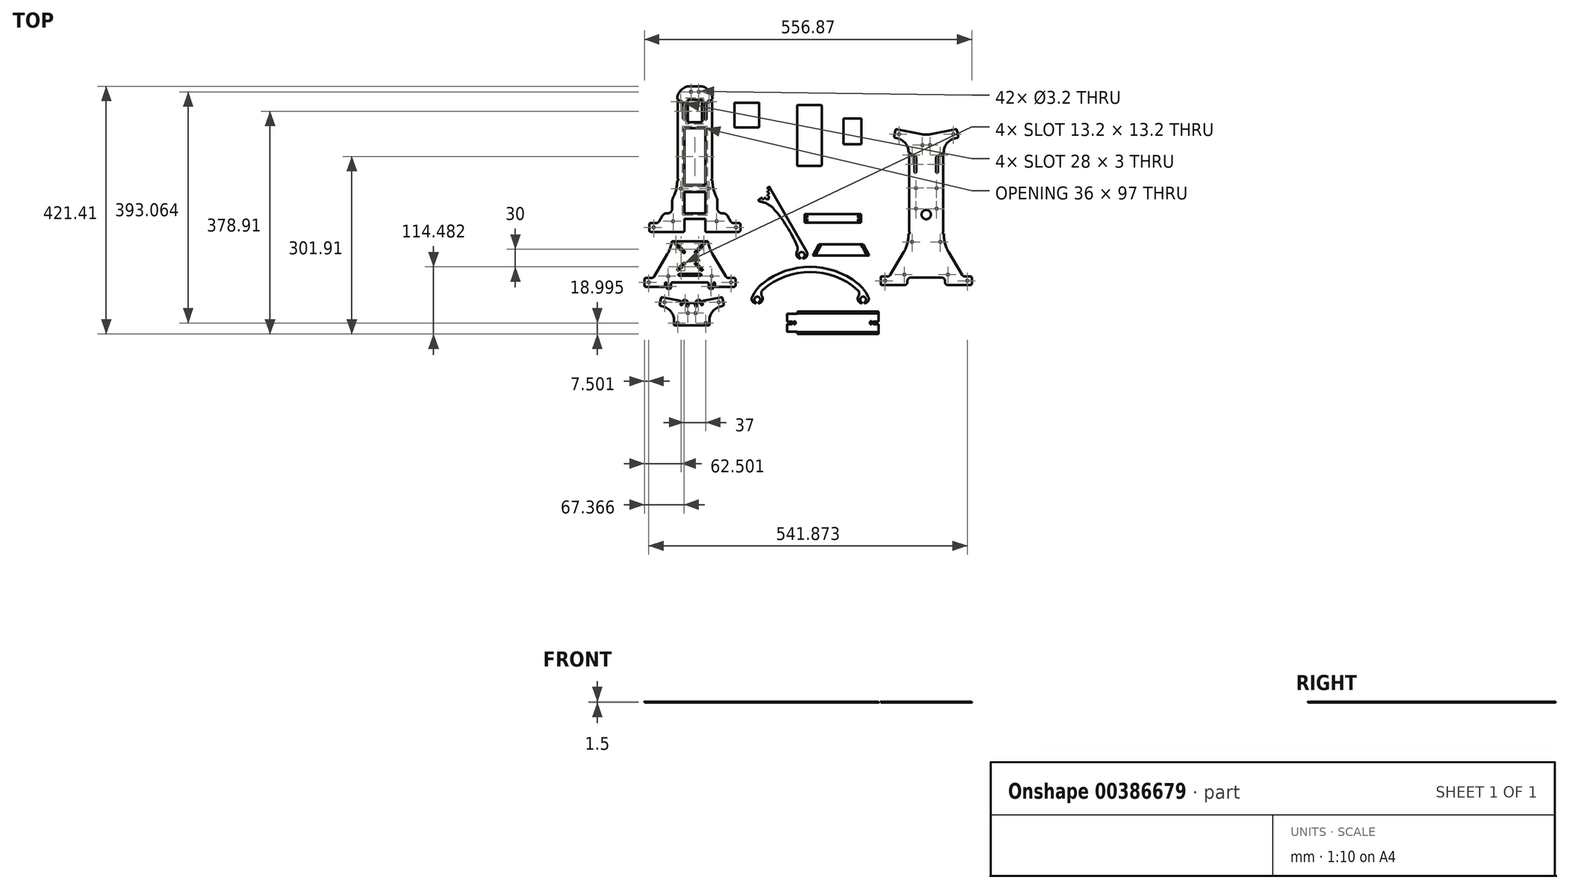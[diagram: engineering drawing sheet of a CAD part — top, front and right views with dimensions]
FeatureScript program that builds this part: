
annotation { "Feature Type Name" : "Feature", "Feature Type Description" : "" }
export const myFeature = defineFeature(function(context is Context, id is Id, definition is map)
    precondition{}
    {
        {
            var Q0;
            Q0=qCreatedBy(makeId("Top.planeOp"),FACE);
            var sketch = newSketch(context, id + "F0", { "sketchPlane" : qUnion([Q0])});
            skCircle(sketch, "E0", {"center": v(204.33, 96.17) * mm, "radius": 1.6 * mm});
            skCircle(sketch, "E1", {"center": v(204.33, 61.17) * mm, "radius": 1.6 * mm});
            skCircle(sketch, "E2", {"center": v(162.83, 152.67) * mm, "radius": 1.6 * mm});
            skCircle(sketch, "E3", {"center": v(162.83, 4.67) * mm, "radius": 1.6 * mm});
            skCircle(sketch, "E4", {"center": v(186.83, 51.17) * mm, "radius": 8 * mm});
            skCircle(sketch, "E5", {"center": v(180.33, 169.32) * mm, "radius": 1.6 * mm});
            skCircle(sketch, "E6", {"center": v(193.33, 169.32) * mm, "radius": 1.6 * mm});
            skCircle(sketch, "E7", {"center": v(223.83, -50.83) * mm, "radius": 1.6 * mm});
            skCircle(sketch, "E8", {"center": v(233, 187.9) * mm, "radius": 1.6 * mm});
            skCircle(sketch, "E9", {"center": v(140.66, 187.9) * mm, "radius": 1.6 * mm});
            skLineSegment(sketch, "E10", {"start": v(154.83, -63.83) * mm, "end": v(154.83, -63.83) * mm});
            skArc(sketch, "E11", {"start": v(149.83, -68.83) * mm, "mid": v(153.37, -67.36) * mm, "end": v(154.83, -63.83) * mm});
            skLineSegment(sketch, "E12", {"start": v(111.83, -68.83) * mm, "end": v(149.83, -68.83) * mm});
            skArc(sketch, "E13", {"start": v(109.33, -66.33) * mm, "mid": v(110.07, -68.1) * mm, "end": v(111.83, -68.83) * mm});
            skLineSegment(sketch, "E14", {"start": v(109.33, -56.33) * mm, "end": v(109.33, -66.33) * mm});
            skArc(sketch, "E15", {"start": v(111.83, -53.83) * mm, "mid": v(110.07, -54.56) * mm, "end": v(109.33, -56.33) * mm});
            skLineSegment(sketch, "E16", {"start": v(121.48, -53.83) * mm, "end": v(111.83, -53.83) * mm});
            skArc(sketch, "E17", {"start": v(121.48, -53.83) * mm, "mid": v(123.96, -53.17) * mm, "end": v(125.78, -51.37) * mm});
            skLineSegment(sketch, "E18", {"start": v(148.49, -12.95) * mm, "end": v(125.78, -51.37) * mm});
            skArc(sketch, "E19", {"start": v(148.49, -12.95) * mm, "mid": v(154.7, 1.76) * mm, "end": v(156.83, 17.58) * mm});
            skLineSegment(sketch, "E20", {"start": v(156.83, 18.67) * mm, "end": v(156.83, 17.58) * mm});
            skLineSegment(sketch, "E21", {"start": v(157.88, 18.67) * mm, "end": v(156.83, 18.67) * mm});
            skArc(sketch, "E22", {"start": v(157.88, 18.67) * mm, "mid": v(158.63, 18.98) * mm, "end": v(158.93, 19.72) * mm});
            skLineSegment(sketch, "E23", {"start": v(158.93, 19.82) * mm, "end": v(158.93, 19.72) * mm});
            skArc(sketch, "E24", {"start": v(158.93, 19.82) * mm, "mid": v(158.63, 20.57) * mm, "end": v(157.88, 20.87) * mm});
            skLineSegment(sketch, "E25", {"start": v(157.83, 20.87) * mm, "end": v(157.88, 20.87) * mm});
            skLineSegment(sketch, "E26", {"start": v(157.83, 154.47) * mm, "end": v(157.83, 20.87) * mm});
            skLineSegment(sketch, "E27", {"start": v(157.88, 154.47) * mm, "end": v(157.83, 154.47) * mm});
            skArc(sketch, "E28", {"start": v(157.88, 154.47) * mm, "mid": v(158.63, 154.78) * mm, "end": v(158.93, 155.52) * mm});
            skLineSegment(sketch, "E29", {"start": v(158.93, 155.62) * mm, "end": v(158.93, 155.52) * mm});
            skArc(sketch, "E30", {"start": v(158.93, 155.62) * mm, "mid": v(158.63, 156.37) * mm, "end": v(157.88, 156.67) * mm});
            skLineSegment(sketch, "E31", {"start": v(156.83, 156.67) * mm, "end": v(157.88, 156.67) * mm});
            skLineSegment(sketch, "E32", {"start": v(156.83, 157.35) * mm, "end": v(156.83, 156.67) * mm});
            skArc(sketch, "E33", {"start": v(156.83, 157.35) * mm, "mid": v(151.4, 172.57) * mm, "end": v(137.54, 180.88) * mm});
            skLineSegment(sketch, "E34", {"start": v(134.28, 181.54) * mm, "end": v(137.54, 180.88) * mm});
            skArc(sketch, "E35", {"start": v(132.32, 184.48) * mm, "mid": v(132.7, 182.6) * mm, "end": v(134.28, 181.54) * mm});
            skLineSegment(sketch, "E36", {"start": v(134.28, 194.28) * mm, "end": v(132.32, 184.48) * mm});
            skArc(sketch, "E37", {"start": v(137.23, 196.24) * mm, "mid": v(135.35, 195.87) * mm, "end": v(134.28, 194.28) * mm});
            skLineSegment(sketch, "E38", {"start": v(178.99, 187.9) * mm, "end": v(137.23, 196.24) * mm});
            skArc(sketch, "E39", {"start": v(178.99, 187.9) * mm, "mid": v(186.83, 187.12) * mm, "end": v(194.68, 187.9) * mm});
            skLineSegment(sketch, "E40", {"start": v(236.44, 196.24) * mm, "end": v(194.68, 187.9) * mm});
            skArc(sketch, "E41", {"start": v(239.38, 194.28) * mm, "mid": v(238.32, 195.87) * mm, "end": v(236.44, 196.24) * mm});
            skLineSegment(sketch, "E42", {"start": v(241.34, 184.48) * mm, "end": v(239.38, 194.28) * mm});
            skArc(sketch, "E43", {"start": v(239.38, 181.54) * mm, "mid": v(240.97, 182.6) * mm, "end": v(241.34, 184.48) * mm});
            skLineSegment(sketch, "E44", {"start": v(236.13, 180.88) * mm, "end": v(239.38, 181.54) * mm});
            skArc(sketch, "E45", {"start": v(236.13, 180.88) * mm, "mid": v(222.27, 172.57) * mm, "end": v(216.83, 157.35) * mm});
            skLineSegment(sketch, "E46", {"start": v(216.83, 156.67) * mm, "end": v(216.83, 157.35) * mm});
            skLineSegment(sketch, "E47", {"start": v(215.78, 156.67) * mm, "end": v(216.83, 156.67) * mm});
            skArc(sketch, "E48", {"start": v(215.78, 156.67) * mm, "mid": v(215.04, 156.37) * mm, "end": v(214.73, 155.62) * mm});
            skLineSegment(sketch, "E49", {"start": v(214.73, 155.52) * mm, "end": v(214.73, 155.62) * mm});
            skArc(sketch, "E50", {"start": v(214.73, 155.52) * mm, "mid": v(215.04, 154.78) * mm, "end": v(215.78, 154.47) * mm});
            skLineSegment(sketch, "E51", {"start": v(215.83, 154.47) * mm, "end": v(215.78, 154.47) * mm});
            skLineSegment(sketch, "E52", {"start": v(215.83, 20.87) * mm, "end": v(215.83, 154.47) * mm});
            skLineSegment(sketch, "E53", {"start": v(215.78, 20.87) * mm, "end": v(215.83, 20.87) * mm});
            skArc(sketch, "E54", {"start": v(215.78, 20.87) * mm, "mid": v(215.04, 20.57) * mm, "end": v(214.73, 19.82) * mm});
            skLineSegment(sketch, "E55", {"start": v(214.73, 19.72) * mm, "end": v(214.73, 19.82) * mm});
            skArc(sketch, "E56", {"start": v(214.73, 19.72) * mm, "mid": v(215.04, 18.98) * mm, "end": v(215.78, 18.67) * mm});
            skLineSegment(sketch, "E57", {"start": v(216.83, 18.67) * mm, "end": v(215.78, 18.67) * mm});
            skLineSegment(sketch, "E58", {"start": v(216.83, 17.58) * mm, "end": v(216.83, 18.67) * mm});
            skArc(sketch, "E59", {"start": v(216.83, 17.58) * mm, "mid": v(218.96, 1.76) * mm, "end": v(225.18, -12.95) * mm});
            skLineSegment(sketch, "E60", {"start": v(247.88, -51.37) * mm, "end": v(225.18, -12.95) * mm});
            skArc(sketch, "E61", {"start": v(247.88, -51.37) * mm, "mid": v(249.7, -53.17) * mm, "end": v(252.19, -53.83) * mm});
            skLineSegment(sketch, "E62", {"start": v(261.83, -53.83) * mm, "end": v(252.19, -53.83) * mm});
            skArc(sketch, "E63", {"start": v(264.33, -56.33) * mm, "mid": v(263.6, -54.56) * mm, "end": v(261.83, -53.83) * mm});
            skLineSegment(sketch, "E64", {"start": v(264.33, -66.33) * mm, "end": v(264.33, -56.33) * mm});
            skArc(sketch, "E65", {"start": v(261.83, -68.83) * mm, "mid": v(263.6, -68.1) * mm, "end": v(264.33, -66.33) * mm});
            skLineSegment(sketch, "E66", {"start": v(223.83, -68.83) * mm, "end": v(261.83, -68.83) * mm});
            skArc(sketch, "E67", {"start": v(218.83, -63.83) * mm, "mid": v(220.3, -67.36) * mm, "end": v(223.83, -68.83) * mm});
            skCircle(sketch, "E68", {"center": v(116.83, -61.33) * mm, "radius": 1.6 * mm});
            skCircle(sketch, "E69", {"center": v(256.83, -61.33) * mm, "radius": 1.6 * mm});
            skCircle(sketch, "E70", {"center": v(149.83, -50.83) * mm, "radius": 1.6 * mm});
            skLineSegment(sketch, "E71", {"start": v(203.83, 148.67) * mm, "end": v(203.83, 123.67) * mm});
            skArc(sketch, "E72", {"start": v(203.83, 123.67) * mm, "mid": v(205.33, 122.17) * mm, "end": v(206.83, 123.67) * mm});
            skLineSegment(sketch, "E73", {"start": v(206.83, 123.67) * mm, "end": v(206.83, 148.67) * mm});
            skArc(sketch, "E74", {"start": v(206.83, 148.67) * mm, "mid": v(205.33, 150.17) * mm, "end": v(203.83, 148.67) * mm});
            skLineSegment(sketch, "E75", {"start": v(169.83, 123.67) * mm, "end": v(169.83, 148.67) * mm});
            skArc(sketch, "E76", {"start": v(169.83, 148.67) * mm, "mid": v(168.33, 150.17) * mm, "end": v(166.83, 148.67) * mm});
            skLineSegment(sketch, "E77", {"start": v(166.83, 148.67) * mm, "end": v(166.83, 123.67) * mm});
            skArc(sketch, "E78", {"start": v(166.83, 123.67) * mm, "mid": v(168.33, 122.17) * mm, "end": v(169.83, 123.67) * mm});
            skCircle(sketch, "E79", {"center": v(210.83, 4.67) * mm, "radius": 1.6 * mm});
            skCircle(sketch, "E80", {"center": v(210.83, 152.67) * mm, "radius": 1.6 * mm});
            skCircle(sketch, "E81", {"center": v(169.33, 61.17) * mm, "radius": 1.6 * mm});
            skCircle(sketch, "E82", {"center": v(169.33, 96.17) * mm, "radius": 1.6 * mm});
            skArc(sketch, "E83", {"start": v(-8.67, 134.54) * mm, "mid": v(-8.32, 133.7) * mm, "end": v(-7.47, 133.34) * mm});
            skLineSegment(sketch, "E84", {"start": v(14.13, 133.34) * mm, "end": v(-7.47, 133.34) * mm});
            skLineSegment(sketch, "E85", {"start": v(-7.47, 133.34) * mm, "end": v(14.13, 133.34) * mm});
            skArc(sketch, "E86", {"start": v(14.13, 133.34) * mm, "mid": v(14.97, 133.7) * mm, "end": v(15.33, 134.54) * mm});
            skLineSegment(sketch, "E87", {"start": v(15.33, 170.14) * mm, "end": v(15.33, 134.54) * mm});
            skLineSegment(sketch, "E88", {"start": v(15.33, 134.54) * mm, "end": v(15.33, 170.14) * mm});
            skArc(sketch, "E89", {"start": v(15.33, 170.14) * mm, "mid": v(14.97, 170.99) * mm, "end": v(14.13, 171.34) * mm});
            skLineSegment(sketch, "E90", {"start": v(-7.47, 171.34) * mm, "end": v(14.13, 171.34) * mm});
            skLineSegment(sketch, "E91", {"start": v(14.13, 171.34) * mm, "end": v(-7.47, 171.34) * mm});
            skArc(sketch, "E92", {"start": v(-7.47, 171.34) * mm, "mid": v(-8.32, 170.99) * mm, "end": v(-8.67, 170.14) * mm});
            skLineSegment(sketch, "E93", {"start": v(-8.67, 134.54) * mm, "end": v(-8.67, 170.14) * mm});
            skLineSegment(sketch, "E94", {"start": v(-8.67, 170.14) * mm, "end": v(-8.67, 134.54) * mm});
            skArc(sketch, "E95", {"start": v(-14.67, 27.54) * mm, "mid": v(-14.32, 26.7) * mm, "end": v(-13.47, 26.34) * mm});
            skLineSegment(sketch, "E96", {"start": v(20.13, 26.34) * mm, "end": v(-13.47, 26.34) * mm});
            skLineSegment(sketch, "E97", {"start": v(-13.47, 26.34) * mm, "end": v(20.13, 26.34) * mm});
            skArc(sketch, "E98", {"start": v(20.13, 26.34) * mm, "mid": v(20.97, 26.7) * mm, "end": v(21.33, 27.54) * mm});
            skLineSegment(sketch, "E99", {"start": v(21.33, 122.14) * mm, "end": v(21.33, 27.54) * mm});
            skLineSegment(sketch, "E100", {"start": v(21.33, 27.54) * mm, "end": v(21.33, 122.14) * mm});
            skArc(sketch, "E101", {"start": v(21.33, 122.14) * mm, "mid": v(20.97, 122.99) * mm, "end": v(20.13, 123.34) * mm});
            skLineSegment(sketch, "E102", {"start": v(-13.47, 123.34) * mm, "end": v(20.13, 123.34) * mm});
            skLineSegment(sketch, "E103", {"start": v(20.13, 123.34) * mm, "end": v(-13.47, 123.34) * mm});
            skArc(sketch, "E104", {"start": v(-13.47, 123.34) * mm, "mid": v(-14.32, 122.99) * mm, "end": v(-14.67, 122.14) * mm});
            skLineSegment(sketch, "E105", {"start": v(-14.67, 27.54) * mm, "end": v(-14.67, 122.14) * mm});
            skLineSegment(sketch, "E106", {"start": v(-14.67, 122.14) * mm, "end": v(-14.67, 27.54) * mm});
            skArc(sketch, "E107", {"start": v(-14.67, -20.46) * mm, "mid": v(-14.32, -21.3) * mm, "end": v(-13.47, -21.66) * mm});
            skLineSegment(sketch, "E108", {"start": v(20.13, -21.66) * mm, "end": v(-13.47, -21.66) * mm});
            skLineSegment(sketch, "E109", {"start": v(-13.47, -21.66) * mm, "end": v(20.13, -21.66) * mm});
            skArc(sketch, "E110", {"start": v(20.13, -21.66) * mm, "mid": v(20.97, -21.3) * mm, "end": v(21.33, -20.46) * mm});
            skLineSegment(sketch, "E111", {"start": v(21.33, 13.14) * mm, "end": v(21.33, -20.46) * mm});
            skLineSegment(sketch, "E112", {"start": v(21.33, -20.46) * mm, "end": v(21.33, 13.14) * mm});
            skArc(sketch, "E113", {"start": v(21.33, 13.14) * mm, "mid": v(20.97, 13.99) * mm, "end": v(20.13, 14.34) * mm});
            skLineSegment(sketch, "E114", {"start": v(-13.47, 14.34) * mm, "end": v(20.13, 14.34) * mm});
            skLineSegment(sketch, "E115", {"start": v(20.13, 14.34) * mm, "end": v(-13.47, 14.34) * mm});
            skArc(sketch, "E116", {"start": v(-13.47, 14.34) * mm, "mid": v(-14.32, 13.99) * mm, "end": v(-14.67, 13.14) * mm});
            skLineSegment(sketch, "E117", {"start": v(-14.67, -20.46) * mm, "end": v(-14.67, 13.14) * mm});
            skLineSegment(sketch, "E118", {"start": v(-14.67, 13.14) * mm, "end": v(-14.67, -20.46) * mm});
            skCircle(sketch, "E119", {"center": v(-20.67, 168.34) * mm, "radius": 1.6 * mm});
            skCircle(sketch, "E120", {"center": v(-20.67, 20.34) * mm, "radius": 1.6 * mm});
            skLineSegment(sketch, "E121", {"start": v(-13.67, 139.34) * mm, "end": v(-13.67, 164.34) * mm});
            skArc(sketch, "E122", {"start": v(-13.67, 164.34) * mm, "mid": v(-15.17, 165.84) * mm, "end": v(-16.67, 164.34) * mm});
            skLineSegment(sketch, "E123", {"start": v(-16.67, 164.34) * mm, "end": v(-16.67, 139.34) * mm});
            skArc(sketch, "E124", {"start": v(-16.67, 139.34) * mm, "mid": v(-15.17, 137.84) * mm, "end": v(-13.67, 139.34) * mm});
            skLineSegment(sketch, "E125", {"start": v(20.33, 164.34) * mm, "end": v(20.33, 139.34) * mm});
            skArc(sketch, "E126", {"start": v(20.33, 139.34) * mm, "mid": v(21.83, 137.84) * mm, "end": v(23.33, 139.34) * mm});
            skLineSegment(sketch, "E127", {"start": v(23.33, 139.34) * mm, "end": v(23.33, 164.34) * mm});
            skArc(sketch, "E128", {"start": v(23.33, 164.34) * mm, "mid": v(21.83, 165.84) * mm, "end": v(20.33, 164.34) * mm});
            skCircle(sketch, "E129", {"center": v(-33.67, -35.16) * mm, "radius": 1.6 * mm});
            skCircle(sketch, "E130", {"center": v(73.33, -45.66) * mm, "radius": 1.6 * mm});
            skLineSegment(sketch, "E131", {"start": v(11.33, 194.34) * mm, "end": v(-4.67, 194.34) * mm});
            skLineSegment(sketch, "E132", {"start": v(-26.67, 172.34) * mm, "end": v(-25.62, 172.34) * mm});
            skArc(sketch, "E133", {"start": v(-4.67, 194.34) * mm, "mid": v(-20.23, 187.9) * mm, "end": v(-26.67, 172.34) * mm});
            skLineSegment(sketch, "E134", {"start": v(-24.57, 171.3) * mm, "end": v(-24.57, 171.2) * mm});
            skArc(sketch, "E135", {"start": v(-24.57, 171.3) * mm, "mid": v(-24.88, 172.03) * mm, "end": v(-25.62, 172.34) * mm});
            skLineSegment(sketch, "E136", {"start": v(-25.62, 170.14) * mm, "end": v(-25.67, 170.14) * mm});
            skArc(sketch, "E137", {"start": v(-25.62, 170.14) * mm, "mid": v(-24.88, 170.45) * mm, "end": v(-24.57, 171.2) * mm});
            skLineSegment(sketch, "E138", {"start": v(-25.67, 170.14) * mm, "end": v(-25.67, 36.54) * mm});
            skLineSegment(sketch, "E139", {"start": v(-25.67, 36.54) * mm, "end": v(-25.62, 36.54) * mm});
            skLineSegment(sketch, "E140", {"start": v(-24.57, 35.5) * mm, "end": v(-24.57, 35.4) * mm});
            skArc(sketch, "E141", {"start": v(-24.57, 35.5) * mm, "mid": v(-24.88, 36.23) * mm, "end": v(-25.62, 36.54) * mm});
            skLineSegment(sketch, "E142", {"start": v(-25.62, 34.34) * mm, "end": v(-26.67, 34.34) * mm});
            skArc(sketch, "E143", {"start": v(-25.62, 34.34) * mm, "mid": v(-24.88, 34.65) * mm, "end": v(-24.57, 35.4) * mm});
            skLineSegment(sketch, "E144", {"start": v(-26.67, 34.34) * mm, "end": v(-26.67, 33.24) * mm});
            skArc(sketch, "E145", {"start": v(-34.04, 4.44) * mm, "mid": v(-28.54, 18.38) * mm, "end": v(-26.67, 33.24) * mm});
            skLineSegment(sketch, "E146", {"start": v(-35.02, 0.6) * mm, "end": v(-35.02, -13.66) * mm});
            skArc(sketch, "E147", {"start": v(-34.04, 4.44) * mm, "mid": v(-34.77, 2.59) * mm, "end": v(-35.02, 0.6) * mm});
            skLineSegment(sketch, "E148", {"start": v(-43.02, -21.66) * mm, "end": v(-44.86, -21.66) * mm});
            skArc(sketch, "E149", {"start": v(-43.02, -21.66) * mm, "mid": v(-37.36, -19.32) * mm, "end": v(-35.02, -13.66) * mm});
            skLineSegment(sketch, "E150", {"start": v(-51.75, -25.59) * mm, "end": v(-57.72, -35.7) * mm});
            skArc(sketch, "E151", {"start": v(-44.86, -21.66) * mm, "mid": v(-48.82, -22.71) * mm, "end": v(-51.75, -25.59) * mm});
            skLineSegment(sketch, "E152", {"start": v(-62.03, -38.16) * mm, "end": v(-71.67, -38.16) * mm});
            skArc(sketch, "E153", {"start": v(-62.03, -38.16) * mm, "mid": v(-59.55, -37.5) * mm, "end": v(-57.72, -35.7) * mm});
            skLineSegment(sketch, "E154", {"start": v(-74.17, -40.66) * mm, "end": v(-74.17, -50.66) * mm});
            skArc(sketch, "E155", {"start": v(-71.67, -38.16) * mm, "mid": v(-73.44, -38.9) * mm, "end": v(-74.17, -40.66) * mm});
            skLineSegment(sketch, "E156", {"start": v(-71.67, -53.16) * mm, "end": v(-15.87, -53.16) * mm});
            skArc(sketch, "E157", {"start": v(-74.17, -50.66) * mm, "mid": v(-73.44, -52.43) * mm, "end": v(-71.67, -53.16) * mm});
            skLineSegment(sketch, "E158", {"start": v(-14.67, -51.96) * mm, "end": v(-14.67, -32.36) * mm});
            skArc(sketch, "E159", {"start": v(-15.87, -53.16) * mm, "mid": v(-15.03, -52.8) * mm, "end": v(-14.67, -51.96) * mm});
            skLineSegment(sketch, "E160", {"start": v(-13.47, -31.16) * mm, "end": v(20.13, -31.16) * mm});
            skArc(sketch, "E161", {"start": v(-13.47, -31.16) * mm, "mid": v(-14.32, -31.51) * mm, "end": v(-14.67, -32.36) * mm});
            skLineSegment(sketch, "E162", {"start": v(21.33, -32.36) * mm, "end": v(21.33, -51.96) * mm});
            skArc(sketch, "E163", {"start": v(21.33, -32.36) * mm, "mid": v(20.97, -31.51) * mm, "end": v(20.13, -31.16) * mm});
            skLineSegment(sketch, "E164", {"start": v(22.53, -53.16) * mm, "end": v(78.33, -53.16) * mm});
            skArc(sketch, "E165", {"start": v(21.33, -51.96) * mm, "mid": v(21.68, -52.8) * mm, "end": v(22.53, -53.16) * mm});
            skLineSegment(sketch, "E166", {"start": v(80.83, -50.66) * mm, "end": v(80.83, -40.66) * mm});
            skArc(sketch, "E167", {"start": v(78.33, -53.16) * mm, "mid": v(80.1, -52.43) * mm, "end": v(80.83, -50.66) * mm});
            skLineSegment(sketch, "E168", {"start": v(78.33, -38.16) * mm, "end": v(68.68, -38.16) * mm});
            skArc(sketch, "E169", {"start": v(80.83, -40.66) * mm, "mid": v(80.1, -38.9) * mm, "end": v(78.33, -38.16) * mm});
            skLineSegment(sketch, "E170", {"start": v(64.37, -35.7) * mm, "end": v(58.4, -25.59) * mm});
            skArc(sketch, "E171", {"start": v(64.37, -35.7) * mm, "mid": v(66.2, -37.5) * mm, "end": v(68.68, -38.16) * mm});
            skLineSegment(sketch, "E172", {"start": v(51.51, -21.66) * mm, "end": v(49.67, -21.66) * mm});
            skArc(sketch, "E173", {"start": v(58.4, -25.59) * mm, "mid": v(55.48, -22.71) * mm, "end": v(51.51, -21.66) * mm});
            skLineSegment(sketch, "E174", {"start": v(41.67, -13.66) * mm, "end": v(41.67, 0.6) * mm});
            skArc(sketch, "E175", {"start": v(41.67, -13.66) * mm, "mid": v(44.01, -19.32) * mm, "end": v(49.67, -21.66) * mm});
            skArc(sketch, "E176", {"start": v(41.67, 0.6) * mm, "mid": v(41.42, 2.59) * mm, "end": v(40.69, 4.44) * mm});
            skLineSegment(sketch, "E177", {"start": v(33.33, 33.24) * mm, "end": v(33.33, 34.34) * mm});
            skArc(sketch, "E178", {"start": v(33.33, 33.24) * mm, "mid": v(35.2, 18.38) * mm, "end": v(40.69, 4.44) * mm});
            skLineSegment(sketch, "E179", {"start": v(33.33, 34.34) * mm, "end": v(32.28, 34.34) * mm});
            skLineSegment(sketch, "E180", {"start": v(31.23, 35.4) * mm, "end": v(31.23, 35.5) * mm});
            skArc(sketch, "E181", {"start": v(31.23, 35.4) * mm, "mid": v(31.53, 34.65) * mm, "end": v(32.28, 34.34) * mm});
            skLineSegment(sketch, "E182", {"start": v(32.28, 36.54) * mm, "end": v(32.33, 36.54) * mm});
            skArc(sketch, "E183", {"start": v(32.28, 36.54) * mm, "mid": v(31.53, 36.23) * mm, "end": v(31.23, 35.5) * mm});
            skLineSegment(sketch, "E184", {"start": v(32.33, 36.54) * mm, "end": v(32.33, 170.14) * mm});
            skLineSegment(sketch, "E185", {"start": v(32.33, 170.14) * mm, "end": v(32.28, 170.14) * mm});
            skLineSegment(sketch, "E186", {"start": v(31.23, 171.2) * mm, "end": v(31.23, 171.3) * mm});
            skArc(sketch, "E187", {"start": v(31.23, 171.2) * mm, "mid": v(31.53, 170.45) * mm, "end": v(32.28, 170.14) * mm});
            skLineSegment(sketch, "E188", {"start": v(32.28, 172.34) * mm, "end": v(33.33, 172.34) * mm});
            skArc(sketch, "E189", {"start": v(32.28, 172.34) * mm, "mid": v(31.53, 172.03) * mm, "end": v(31.23, 171.3) * mm});
            skArc(sketch, "E190", {"start": v(33.33, 172.34) * mm, "mid": v(26.88, 187.9) * mm, "end": v(11.33, 194.34) * mm});
            skCircle(sketch, "E191", {"center": v(-66.67, -45.66) * mm, "radius": 1.6 * mm});
            skCircle(sketch, "E192", {"center": v(40.33, -35.16) * mm, "radius": 1.6 * mm});
            skCircle(sketch, "E193", {"center": v(9.83, 184.99) * mm, "radius": 1.6 * mm});
            skCircle(sketch, "E194", {"center": v(-3.17, 184.99) * mm, "radius": 1.6 * mm});
            skCircle(sketch, "E195", {"center": v(27.33, 20.34) * mm, "radius": 1.6 * mm});
            skCircle(sketch, "E196", {"center": v(27.33, 168.34) * mm, "radius": 1.6 * mm});
            skLineSegment(sketch, "E197", {"start": v(-11.67, 131.54) * mm, "end": v(-11.67, 173.14) * mm});
            skLineSegment(sketch, "E198", {"start": v(17.13, 130.34) * mm, "end": v(-10.47, 130.34) * mm});
            skArc(sketch, "E199", {"start": v(-11.67, 131.54) * mm, "mid": v(-11.32, 130.7) * mm, "end": v(-10.47, 130.34) * mm});
            skLineSegment(sketch, "E200", {"start": v(18.33, 173.14) * mm, "end": v(18.33, 131.54) * mm});
            skArc(sketch, "E201", {"start": v(17.13, 130.34) * mm, "mid": v(17.97, 130.7) * mm, "end": v(18.33, 131.54) * mm});
            skLineSegment(sketch, "E202", {"start": v(-10.47, 174.34) * mm, "end": v(17.13, 174.34) * mm});
            skArc(sketch, "E203", {"start": v(18.33, 173.14) * mm, "mid": v(17.97, 173.99) * mm, "end": v(17.13, 174.34) * mm});
            skArc(sketch, "E204", {"start": v(-10.47, 174.34) * mm, "mid": v(-11.32, 173.99) * mm, "end": v(-11.67, 173.14) * mm});
            skLineSegment(sketch, "E205", {"start": v(24.33, 125.14) * mm, "end": v(24.33, 24.54) * mm});
            skArc(sketch, "E206", {"start": v(23.13, 23.34) * mm, "mid": v(23.97, 23.7) * mm, "end": v(24.33, 24.54) * mm});
            skLineSegment(sketch, "E207", {"start": v(-16.47, 126.34) * mm, "end": v(23.13, 126.34) * mm});
            skArc(sketch, "E208", {"start": v(24.33, 125.14) * mm, "mid": v(23.97, 125.99) * mm, "end": v(23.13, 126.34) * mm});
            skLineSegment(sketch, "E209", {"start": v(-17.67, 24.54) * mm, "end": v(-17.67, 125.14) * mm});
            skArc(sketch, "E210", {"start": v(-16.47, 126.34) * mm, "mid": v(-17.32, 125.99) * mm, "end": v(-17.67, 125.14) * mm});
            skLineSegment(sketch, "E211", {"start": v(23.13, 23.34) * mm, "end": v(-16.47, 23.34) * mm});
            skArc(sketch, "E212", {"start": v(-17.67, 24.54) * mm, "mid": v(-17.32, 23.7) * mm, "end": v(-16.47, 23.34) * mm});
            skLineSegment(sketch, "E213", {"start": v(23.13, -24.66) * mm, "end": v(-16.47, -24.66) * mm});
            skLineSegment(sketch, "E214", {"start": v(24.33, 16.14) * mm, "end": v(24.33, -23.46) * mm});
            skArc(sketch, "E215", {"start": v(23.13, -24.66) * mm, "mid": v(23.97, -24.3) * mm, "end": v(24.33, -23.46) * mm});
            skLineSegment(sketch, "E216", {"start": v(-16.47, 17.34) * mm, "end": v(23.13, 17.34) * mm});
            skArc(sketch, "E217", {"start": v(24.33, 16.14) * mm, "mid": v(23.97, 16.99) * mm, "end": v(23.13, 17.34) * mm});
            skLineSegment(sketch, "E218", {"start": v(-17.67, -23.46) * mm, "end": v(-17.67, 16.14) * mm});
            skArc(sketch, "E219", {"start": v(-16.47, 17.34) * mm, "mid": v(-17.32, 16.99) * mm, "end": v(-17.67, 16.14) * mm});
            skArc(sketch, "E220", {"start": v(-17.67, -23.46) * mm, "mid": v(-17.32, -24.3) * mm, "end": v(-16.47, -24.66) * mm});
            skLineSegment(sketch, "E221", {"start": v(-28.63, -131.82) * mm, "end": v(-28.63, -133.82) * mm});
            skLineSegment(sketch, "E222", {"start": v(-25.43, -133.82) * mm, "end": v(-25.43, -131.82) * mm});
            skArc(sketch, "E223", {"start": v(-28.63, -133.82) * mm, "mid": v(-27.03, -135.42) * mm, "end": v(-25.43, -133.82) * mm});
            skLineSegment(sketch, "E224", {"start": v(104.57, -133.82) * mm, "end": v(104.57, -131.82) * mm});
            skArc(sketch, "E225", {"start": v(-25.43, -131.82) * mm, "mid": v(-27.03, -130.22) * mm, "end": v(-28.63, -131.82) * mm});
            skLineSegment(sketch, "E226", {"start": v(101.37, -131.82) * mm, "end": v(101.37, -133.82) * mm});
            skArc(sketch, "E227", {"start": v(104.57, -131.82) * mm, "mid": v(102.97, -130.22) * mm, "end": v(101.37, -131.82) * mm});
            skArc(sketch, "E228", {"start": v(101.37, -133.82) * mm, "mid": v(102.97, -135.42) * mm, "end": v(104.57, -133.82) * mm});
            skLineSegment(sketch, "E229", {"start": v(115.97, -117.07) * mm, "end": v(-22.26, -117.07) * mm});
            skArc(sketch, "E230", {"start": v(-23.23, -117.57) * mm, "mid": v(-22.69, -117.44) * mm, "end": v(-22.26, -117.07) * mm});
            skLineSegment(sketch, "E231", {"start": v(115.97, -129.37) * mm, "end": v(115.97, -117.07) * mm});
            skLineSegment(sketch, "E232", {"start": v(107.97, -130.57) * mm, "end": v(114.77, -130.57) * mm});
            skArc(sketch, "E233", {"start": v(114.77, -130.57) * mm, "mid": v(115.61, -130.22) * mm, "end": v(115.97, -129.37) * mm});
            skLineSegment(sketch, "E234", {"start": v(114.77, -135.07) * mm, "end": v(107.97, -135.07) * mm});
            skArc(sketch, "E235", {"start": v(107.97, -130.57) * mm, "mid": v(105.72, -132.82) * mm, "end": v(107.97, -135.07) * mm});
            skLineSegment(sketch, "E236", {"start": v(115.97, -148.57) * mm, "end": v(115.97, -136.27) * mm});
            skArc(sketch, "E237", {"start": v(115.97, -136.27) * mm, "mid": v(115.61, -135.43) * mm, "end": v(114.77, -135.07) * mm});
            skLineSegment(sketch, "E238", {"start": v(-22.26, -148.57) * mm, "end": v(115.97, -148.57) * mm});
            skLineSegment(sketch, "E239", {"start": v(-38.83, -148.07) * mm, "end": v(-23.23, -148.07) * mm});
            skArc(sketch, "E240", {"start": v(-22.26, -148.57) * mm, "mid": v(-22.69, -148.2) * mm, "end": v(-23.23, -148.07) * mm});
            skLineSegment(sketch, "E241", {"start": v(-40.03, -136.27) * mm, "end": v(-40.03, -146.87) * mm});
            skArc(sketch, "E242", {"start": v(-40.03, -146.87) * mm, "mid": v(-39.68, -147.72) * mm, "end": v(-38.83, -148.07) * mm});
            skLineSegment(sketch, "E243", {"start": v(-32.03, -135.07) * mm, "end": v(-38.83, -135.07) * mm});
            skArc(sketch, "E244", {"start": v(-38.83, -135.07) * mm, "mid": v(-39.68, -135.43) * mm, "end": v(-40.03, -136.27) * mm});
            skLineSegment(sketch, "E245", {"start": v(-38.83, -130.57) * mm, "end": v(-32.03, -130.57) * mm});
            skArc(sketch, "E246", {"start": v(-32.03, -135.07) * mm, "mid": v(-29.78, -132.82) * mm, "end": v(-32.03, -130.57) * mm});
            skLineSegment(sketch, "E247", {"start": v(-40.03, -118.77) * mm, "end": v(-40.03, -129.37) * mm});
            skArc(sketch, "E248", {"start": v(-40.03, -129.37) * mm, "mid": v(-39.68, -130.22) * mm, "end": v(-38.83, -130.57) * mm});
            skLineSegment(sketch, "E249", {"start": v(-23.23, -117.57) * mm, "end": v(-38.83, -117.57) * mm});
            skArc(sketch, "E250", {"start": v(-38.83, -117.57) * mm, "mid": v(-39.68, -117.93) * mm, "end": v(-40.03, -118.77) * mm});
            skLineSegment(sketch, "E251", {"start": v(115.97, -115.57) * mm, "end": v(115.97, -114.77) * mm});
            skLineSegment(sketch, "E252", {"start": v(-22.03, -115.57) * mm, "end": v(115.97, -115.57) * mm});
            skLineSegment(sketch, "E253", {"start": v(-22.03, -114.77) * mm, "end": v(-22.03, -115.57) * mm});
            skLineSegment(sketch, "E254", {"start": v(114.77, -113.57) * mm, "end": v(-20.83, -113.57) * mm});
            skArc(sketch, "E255", {"start": v(-20.83, -113.57) * mm, "mid": v(-21.68, -113.93) * mm, "end": v(-22.03, -114.77) * mm});
            skArc(sketch, "E256", {"start": v(115.97, -114.77) * mm, "mid": v(115.61, -113.93) * mm, "end": v(114.77, -113.57) * mm});
            skLineSegment(sketch, "E257", {"start": v(115.97, -129.37) * mm, "end": v(115.97, -114.77) * mm});
            skLineSegment(sketch, "E258", {"start": v(-22.03, -114.77) * mm, "end": v(-22.03, -116.37) * mm});
            skArc(sketch, "E259", {"start": v(-23.23, -117.57) * mm, "mid": v(-22.39, -117.22) * mm, "end": v(-22.03, -116.37) * mm});
            skLineSegment(sketch, "E260", {"start": v(-22.03, -149.27) * mm, "end": v(-22.03, -150.87) * mm});
            skArc(sketch, "E261", {"start": v(-22.03, -149.27) * mm, "mid": v(-22.39, -148.43) * mm, "end": v(-23.23, -148.07) * mm});
            skLineSegment(sketch, "E262", {"start": v(-20.83, -152.07) * mm, "end": v(114.77, -152.07) * mm});
            skArc(sketch, "E263", {"start": v(-22.03, -150.87) * mm, "mid": v(-21.68, -151.72) * mm, "end": v(-20.83, -152.07) * mm});
            skLineSegment(sketch, "E264", {"start": v(115.97, -150.87) * mm, "end": v(115.97, -136.27) * mm});
            skArc(sketch, "E265", {"start": v(114.77, -152.07) * mm, "mid": v(115.61, -151.72) * mm, "end": v(115.97, -150.87) * mm});
            skLineSegment(sketch, "E266", {"start": v(-22.03, -150.07) * mm, "end": v(-22.03, -150.87) * mm});
            skLineSegment(sketch, "E267", {"start": v(115.97, -150.07) * mm, "end": v(-22.03, -150.07) * mm});
            skLineSegment(sketch, "E268", {"start": v(115.97, -150.87) * mm, "end": v(115.97, -150.07) * mm});
            skLineSegment(sketch, "E269", {"start": v(115.97, -115.57) * mm, "end": v(115.97, -117.07) * mm});
            skLineSegment(sketch, "E270", {"start": v(-22.03, -116.37) * mm, "end": v(-22.03, -115.57) * mm});
            skArc(sketch, "E271", {"start": v(-22.26, -117.07) * mm, "mid": v(-22.1, -116.74) * mm, "end": v(-22.03, -116.37) * mm});
            skArc(sketch, "E272", {"start": v(-22.03, -149.27) * mm, "mid": v(-22.1, -148.9) * mm, "end": v(-22.26, -148.57) * mm});
            skLineSegment(sketch, "E273", {"start": v(-22.03, -150.07) * mm, "end": v(-22.03, -149.27) * mm});
            skLineSegment(sketch, "E274", {"start": v(115.97, -148.57) * mm, "end": v(115.97, -150.07) * mm});
            skCircle(sketch, "E275", {"center": v(-209.04, 1.91) * mm, "radius": 1.6 * mm});
            skLineSegment(sketch, "E276", {"start": v(-167.04, -49.59) * mm, "end": v(-203.04, -49.59) * mm});
            skArc(sketch, "E277", {"start": v(-203.04, -49.59) * mm, "mid": v(-204.64, -51.19) * mm, "end": v(-203.04, -52.79) * mm});
            skLineSegment(sketch, "E278", {"start": v(-203.04, -52.79) * mm, "end": v(-167.04, -52.79) * mm});
            skArc(sketch, "E279", {"start": v(-167.04, -52.79) * mm, "mid": v(-165.44, -51.19) * mm, "end": v(-167.04, -49.59) * mm});
            skLineSegment(sketch, "E280", {"start": v(-196.17, -31.46) * mm, "end": v(-206.17, -41.46) * mm});
            skArc(sketch, "E281", {"start": v(-206.17, -41.46) * mm, "mid": v(-206.17, -43.72) * mm, "end": v(-203.9, -43.72) * mm});
            skLineSegment(sketch, "E282", {"start": v(-203.9, -43.72) * mm, "end": v(-193.9, -33.72) * mm});
            skArc(sketch, "E283", {"start": v(-193.9, -33.72) * mm, "mid": v(-193.9, -31.46) * mm, "end": v(-196.17, -31.46) * mm});
            skCircle(sketch, "E284", {"center": v(-222.04, -53.59) * mm, "radius": 1.6 * mm});
            skCircle(sketch, "E285", {"center": v(-148.04, -53.59) * mm, "radius": 1.6 * mm});
            skCircle(sketch, "E286", {"center": v(-255.04, -64.09) * mm, "radius": 1.6 * mm});
            skCircle(sketch, "E287", {"center": v(-149.04, -71.09) * mm, "radius": 1.6 * mm});
            skLineSegment(sketch, "E288", {"start": v(-154.38, 5.91) * mm, "end": v(-215.7, 5.91) * mm});
            skArc(sketch, "E289", {"start": v(-154.38, 5.91) * mm, "mid": v(-151.58, -5.27) * mm, "end": v(-146.7, -15.7) * mm});
            skLineSegment(sketch, "E290", {"start": v(-124, -54.13) * mm, "end": v(-146.7, -15.7) * mm});
            skArc(sketch, "E291", {"start": v(-124, -54.13) * mm, "mid": v(-122.16, -55.93) * mm, "end": v(-119.69, -56.59) * mm});
            skLineSegment(sketch, "E292", {"start": v(-110.04, -56.59) * mm, "end": v(-119.69, -56.59) * mm});
            skArc(sketch, "E293", {"start": v(-107.54, -59.09) * mm, "mid": v(-108.27, -57.32) * mm, "end": v(-110.04, -56.59) * mm});
            skLineSegment(sketch, "E294", {"start": v(-107.54, -69.09) * mm, "end": v(-107.54, -59.09) * mm});
            skArc(sketch, "E295", {"start": v(-110.04, -71.59) * mm, "mid": v(-108.27, -70.86) * mm, "end": v(-107.54, -69.09) * mm});
            skLineSegment(sketch, "E296", {"start": v(-141.34, -71.59) * mm, "end": v(-110.04, -71.59) * mm});
            skArc(sketch, "E297", {"start": v(-142.54, -70.39) * mm, "mid": v(-142.19, -71.24) * mm, "end": v(-141.34, -71.59) * mm});
            skLineSegment(sketch, "E298", {"start": v(-142.54, -65.54) * mm, "end": v(-142.54, -70.39) * mm});
            skArc(sketch, "E299", {"start": v(-142.54, -65.54) * mm, "mid": v(-142.9, -64.69) * mm, "end": v(-143.74, -64.34) * mm});
            skLineSegment(sketch, "E300", {"start": v(-143.84, -64.34) * mm, "end": v(-143.74, -64.34) * mm});
            skArc(sketch, "E301", {"start": v(-143.84, -64.34) * mm, "mid": v(-144.69, -64.69) * mm, "end": v(-145.04, -65.54) * mm});
            skLineSegment(sketch, "E302", {"start": v(-145.04, -72.59) * mm, "end": v(-145.04, -65.54) * mm});
            skArc(sketch, "E303", {"start": v(-147.54, -75.09) * mm, "mid": v(-145.77, -74.36) * mm, "end": v(-145.04, -72.59) * mm});
            skLineSegment(sketch, "E304", {"start": v(-150.54, -75.09) * mm, "end": v(-147.54, -75.09) * mm});
            skArc(sketch, "E305", {"start": v(-153.04, -72.59) * mm, "mid": v(-152.3, -74.36) * mm, "end": v(-150.54, -75.09) * mm});
            skLineSegment(sketch, "E306", {"start": v(-153.04, -66.59) * mm, "end": v(-153.04, -72.59) * mm});
            skArc(sketch, "E307", {"start": v(-153.04, -66.59) * mm, "mid": v(-153.77, -64.82) * mm, "end": v(-155.54, -64.09) * mm});
            skLineSegment(sketch, "E308", {"start": v(-214.54, -64.09) * mm, "end": v(-155.54, -64.09) * mm});
            skArc(sketch, "E309", {"start": v(-214.54, -64.09) * mm, "mid": v(-216.3, -64.82) * mm, "end": v(-217.04, -66.59) * mm});
            skLineSegment(sketch, "E310", {"start": v(-217.04, -72.59) * mm, "end": v(-217.04, -66.59) * mm});
            skArc(sketch, "E311", {"start": v(-219.54, -75.09) * mm, "mid": v(-217.77, -74.36) * mm, "end": v(-217.04, -72.59) * mm});
            skLineSegment(sketch, "E312", {"start": v(-222.54, -75.09) * mm, "end": v(-219.54, -75.09) * mm});
            skArc(sketch, "E313", {"start": v(-225.04, -72.59) * mm, "mid": v(-224.3, -74.36) * mm, "end": v(-222.54, -75.09) * mm});
            skLineSegment(sketch, "E314", {"start": v(-225.04, -65.54) * mm, "end": v(-225.04, -72.59) * mm});
            skArc(sketch, "E315", {"start": v(-225.04, -65.54) * mm, "mid": v(-225.4, -64.69) * mm, "end": v(-226.24, -64.34) * mm});
            skLineSegment(sketch, "E316", {"start": v(-226.34, -64.34) * mm, "end": v(-226.24, -64.34) * mm});
            skArc(sketch, "E317", {"start": v(-226.34, -64.34) * mm, "mid": v(-227.19, -64.69) * mm, "end": v(-227.54, -65.54) * mm});
            skLineSegment(sketch, "E318", {"start": v(-227.54, -70.39) * mm, "end": v(-227.54, -65.54) * mm});
            skArc(sketch, "E319", {"start": v(-228.74, -71.59) * mm, "mid": v(-227.9, -71.24) * mm, "end": v(-227.54, -70.39) * mm});
            skLineSegment(sketch, "E320", {"start": v(-260.04, -71.59) * mm, "end": v(-228.74, -71.59) * mm});
            skArc(sketch, "E321", {"start": v(-262.54, -69.09) * mm, "mid": v(-261.8, -70.86) * mm, "end": v(-260.04, -71.59) * mm});
            skLineSegment(sketch, "E322", {"start": v(-262.54, -59.09) * mm, "end": v(-262.54, -69.09) * mm});
            skArc(sketch, "E323", {"start": v(-260.04, -56.59) * mm, "mid": v(-261.8, -57.32) * mm, "end": v(-262.54, -59.09) * mm});
            skLineSegment(sketch, "E324", {"start": v(-250.4, -56.59) * mm, "end": v(-260.04, -56.59) * mm});
            skArc(sketch, "E325", {"start": v(-250.4, -56.59) * mm, "mid": v(-247.91, -55.93) * mm, "end": v(-246.09, -54.13) * mm});
            skLineSegment(sketch, "E326", {"start": v(-223.38, -15.7) * mm, "end": v(-246.09, -54.13) * mm});
            skArc(sketch, "E327", {"start": v(-223.38, -15.7) * mm, "mid": v(-218.5, -5.27) * mm, "end": v(-215.7, 5.91) * mm});
            skCircle(sketch, "E328", {"center": v(-221.04, -71.09) * mm, "radius": 1.6 * mm});
            skCircle(sketch, "E329", {"center": v(-115.04, -64.09) * mm, "radius": 1.6 * mm});
            skLineSegment(sketch, "E330", {"start": v(-173.9, -13.72) * mm, "end": v(-163.9, -3.72) * mm});
            skArc(sketch, "E331", {"start": v(-163.9, -3.72) * mm, "mid": v(-163.9, -1.46) * mm, "end": v(-166.17, -1.46) * mm});
            skLineSegment(sketch, "E332", {"start": v(-166.17, -1.46) * mm, "end": v(-176.17, -11.46) * mm});
            skArc(sketch, "E333", {"start": v(-176.17, -11.46) * mm, "mid": v(-176.17, -13.72) * mm, "end": v(-173.9, -13.72) * mm});
            skArc(sketch, "E334", {"start": v(-203.9, -1.46) * mm, "mid": v(-206.17, -1.46) * mm, "end": v(-206.17, -3.72) * mm});
            skLineSegment(sketch, "E335", {"start": v(-206.17, -3.72) * mm, "end": v(-196.17, -13.72) * mm});
            skArc(sketch, "E336", {"start": v(-196.17, -13.72) * mm, "mid": v(-193.9, -13.72) * mm, "end": v(-193.9, -11.46) * mm});
            skLineSegment(sketch, "E337", {"start": v(-193.9, -11.46) * mm, "end": v(-203.9, -1.46) * mm});
            skArc(sketch, "E338", {"start": v(-166.17, -43.72) * mm, "mid": v(-163.9, -43.72) * mm, "end": v(-163.9, -41.46) * mm});
            skLineSegment(sketch, "E339", {"start": v(-163.9, -41.46) * mm, "end": v(-173.9, -31.46) * mm});
            skArc(sketch, "E340", {"start": v(-173.9, -31.46) * mm, "mid": v(-176.17, -31.46) * mm, "end": v(-176.17, -33.72) * mm});
            skLineSegment(sketch, "E341", {"start": v(-176.17, -33.72) * mm, "end": v(-166.17, -43.72) * mm});
            skCircle(sketch, "E342", {"center": v(-161.04, 1.91) * mm, "radius": 1.6 * mm});
            skCircle(sketch, "E343", {"center": v(-178, -133.07) * mm, "radius": 1.6 * mm});
            skCircle(sketch, "E344", {"center": v(-195.5, -116.43) * mm, "radius": 1.6 * mm});
            skCircle(sketch, "E345", {"center": v(-155.83, -97.84) * mm, "radius": 1.6 * mm});
            skCircle(sketch, "E346", {"center": v(-248.18, -97.84) * mm, "radius": 1.6 * mm});
            skLineSegment(sketch, "E347", {"start": v(-232, -129.22) * mm, "end": v(-232, -137.07) * mm});
            skArc(sketch, "E348", {"start": v(-232, -129.22) * mm, "mid": v(-237.68, -113.37) * mm, "end": v(-252.1, -104.7) * mm});
            skLineSegment(sketch, "E349", {"start": v(-254.56, -104.21) * mm, "end": v(-252.1, -104.7) * mm});
            skArc(sketch, "E350", {"start": v(-256.52, -101.27) * mm, "mid": v(-256.15, -103.15) * mm, "end": v(-254.56, -104.21) * mm});
            skLineSegment(sketch, "E351", {"start": v(-254.56, -91.47) * mm, "end": v(-256.52, -101.27) * mm});
            skArc(sketch, "E352", {"start": v(-251.62, -89.5) * mm, "mid": v(-253.5, -89.88) * mm, "end": v(-254.56, -91.47) * mm});
            skLineSegment(sketch, "E353", {"start": v(-221.86, -95.46) * mm, "end": v(-251.62, -89.5) * mm});
            skArc(sketch, "E354", {"start": v(-219.9, -98.4) * mm, "mid": v(-220.27, -96.52) * mm, "end": v(-221.86, -95.46) * mm});
            skLineSegment(sketch, "E355", {"start": v(-220.58, -101.83) * mm, "end": v(-219.9, -98.4) * mm});
            skArc(sketch, "E356", {"start": v(-220.58, -101.83) * mm, "mid": v(-219.7, -103.15) * mm, "end": v(-218.37, -102.27) * mm});
            skLineSegment(sketch, "E357", {"start": v(-217.1, -95.9) * mm, "end": v(-218.37, -102.27) * mm});
            skArc(sketch, "E358", {"start": v(-214.16, -93.94) * mm, "mid": v(-216.03, -94.3) * mm, "end": v(-217.1, -95.9) * mm});
            skLineSegment(sketch, "E359", {"start": v(-211.21, -94.53) * mm, "end": v(-214.16, -93.94) * mm});
            skArc(sketch, "E360", {"start": v(-209.25, -97.47) * mm, "mid": v(-209.62, -95.6) * mm, "end": v(-211.21, -94.53) * mm});
            skLineSegment(sketch, "E361", {"start": v(-210.53, -103.84) * mm, "end": v(-209.25, -97.47) * mm});
            skArc(sketch, "E362", {"start": v(-210.53, -103.84) * mm, "mid": v(-209.45, -105.46) * mm, "end": v(-207.83, -104.38) * mm});
            skLineSegment(sketch, "E363", {"start": v(-207.15, -100.95) * mm, "end": v(-207.83, -104.38) * mm});
            skArc(sketch, "E364", {"start": v(-204.2, -98.99) * mm, "mid": v(-206.08, -99.36) * mm, "end": v(-207.15, -100.95) * mm});
            skLineSegment(sketch, "E365", {"start": v(-202.5, -99.33) * mm, "end": v(-204.2, -98.99) * mm});
            skArc(sketch, "E366", {"start": v(-202.5, -99.33) * mm, "mid": v(-202, -99.38) * mm, "end": v(-201.52, -99.33) * mm});
            skLineSegment(sketch, "E367", {"start": v(-199.81, -98.99) * mm, "end": v(-201.52, -99.33) * mm});
            skArc(sketch, "E368", {"start": v(-196.87, -100.95) * mm, "mid": v(-197.94, -99.36) * mm, "end": v(-199.81, -98.99) * mm});
            skLineSegment(sketch, "E369", {"start": v(-196.18, -104.38) * mm, "end": v(-196.87, -100.95) * mm});
            skArc(sketch, "E370", {"start": v(-196.18, -104.38) * mm, "mid": v(-194.57, -105.46) * mm, "end": v(-193.5, -103.84) * mm});
            skLineSegment(sketch, "E371", {"start": v(-194.77, -97.47) * mm, "end": v(-193.5, -103.84) * mm});
            skArc(sketch, "E372", {"start": v(-192.8, -94.53) * mm, "mid": v(-194.4, -95.6) * mm, "end": v(-194.77, -97.47) * mm});
            skLineSegment(sketch, "E373", {"start": v(-189.86, -93.94) * mm, "end": v(-192.8, -94.53) * mm});
            skArc(sketch, "E374", {"start": v(-186.92, -95.9) * mm, "mid": v(-187.98, -94.3) * mm, "end": v(-189.86, -93.94) * mm});
            skLineSegment(sketch, "E375", {"start": v(-185.64, -102.27) * mm, "end": v(-186.92, -95.9) * mm});
            skArc(sketch, "E376", {"start": v(-185.64, -102.27) * mm, "mid": v(-184.32, -103.15) * mm, "end": v(-183.44, -101.83) * mm});
            skLineSegment(sketch, "E377", {"start": v(-184.12, -98.4) * mm, "end": v(-183.44, -101.83) * mm});
            skArc(sketch, "E378", {"start": v(-182.16, -95.46) * mm, "mid": v(-183.75, -96.52) * mm, "end": v(-184.12, -98.4) * mm});
            skLineSegment(sketch, "E379", {"start": v(-152.4, -89.5) * mm, "end": v(-182.16, -95.46) * mm});
            skArc(sketch, "E380", {"start": v(-149.46, -91.47) * mm, "mid": v(-150.53, -89.88) * mm, "end": v(-152.4, -89.5) * mm});
            skLineSegment(sketch, "E381", {"start": v(-147.5, -101.27) * mm, "end": v(-149.46, -91.47) * mm});
            skArc(sketch, "E382", {"start": v(-149.46, -104.21) * mm, "mid": v(-147.87, -103.15) * mm, "end": v(-147.5, -101.27) * mm});
            skLineSegment(sketch, "E383", {"start": v(-151.91, -104.7) * mm, "end": v(-149.46, -104.21) * mm});
            skArc(sketch, "E384", {"start": v(-151.91, -104.7) * mm, "mid": v(-166.34, -113.37) * mm, "end": v(-172, -129.22) * mm});
            skLineSegment(sketch, "E385", {"start": v(-172, -137.07) * mm, "end": v(-172, -129.22) * mm});
            skLineSegment(sketch, "E386", {"start": v(-232, -137.07) * mm, "end": v(-172, -137.07) * mm});
            skCircle(sketch, "E387", {"center": v(-226, -133.07) * mm, "radius": 1.6 * mm});
            skCircle(sketch, "E388", {"center": v(-190.63, -97.66) * mm, "radius": 1.6 * mm});
            skCircle(sketch, "E389", {"center": v(-213.38, -97.66) * mm, "radius": 1.6 * mm});
            skCircle(sketch, "E390", {"center": v(-208.5, -116.43) * mm, "radius": 1.6 * mm});
            skLineSegment(sketch, "E391", {"start": v(-272.85, 165.67) * mm, "end": v(-272.85, 163.67) * mm});
            skLineSegment(sketch, "E392", {"start": v(-269.65, 163.67) * mm, "end": v(-269.65, 165.67) * mm});
            skArc(sketch, "E393", {"start": v(-272.85, 163.67) * mm, "mid": v(-271.25, 162.07) * mm, "end": v(-269.65, 163.67) * mm});
            skLineSegment(sketch, "E394", {"start": v(-139.65, 163.67) * mm, "end": v(-139.65, 165.67) * mm});
            skArc(sketch, "E395", {"start": v(-269.65, 165.67) * mm, "mid": v(-271.25, 167.27) * mm, "end": v(-272.85, 165.67) * mm});
            skLineSegment(sketch, "E396", {"start": v(-142.85, 165.67) * mm, "end": v(-142.85, 163.67) * mm});
            skArc(sketch, "E397", {"start": v(-139.65, 165.67) * mm, "mid": v(-141.25, 167.27) * mm, "end": v(-142.85, 165.67) * mm});
            skArc(sketch, "E398", {"start": v(-142.85, 163.67) * mm, "mid": v(-141.25, 162.07) * mm, "end": v(-139.65, 163.67) * mm});
            skLineSegment(sketch, "E399", {"start": v(-128.25, 180.42) * mm, "end": v(-266.47, 180.42) * mm});
            skArc(sketch, "E400", {"start": v(-267.45, 179.92) * mm, "mid": v(-266.9, 180.05) * mm, "end": v(-266.47, 180.42) * mm});
            skLineSegment(sketch, "E401", {"start": v(-128.25, 168.12) * mm, "end": v(-128.25, 180.42) * mm});
            skLineSegment(sketch, "E402", {"start": v(-136.25, 166.92) * mm, "end": v(-129.45, 166.92) * mm});
            skArc(sketch, "E403", {"start": v(-129.45, 166.92) * mm, "mid": v(-128.6, 167.27) * mm, "end": v(-128.25, 168.12) * mm});
            skLineSegment(sketch, "E404", {"start": v(-129.45, 162.42) * mm, "end": v(-136.25, 162.42) * mm});
            skArc(sketch, "E405", {"start": v(-136.25, 166.92) * mm, "mid": v(-138.5, 164.67) * mm, "end": v(-136.25, 162.42) * mm});
            skLineSegment(sketch, "E406", {"start": v(-128.25, 148.92) * mm, "end": v(-128.25, 161.22) * mm});
            skArc(sketch, "E407", {"start": v(-128.25, 161.22) * mm, "mid": v(-128.6, 162.07) * mm, "end": v(-129.45, 162.42) * mm});
            skLineSegment(sketch, "E408", {"start": v(-266.47, 148.92) * mm, "end": v(-128.25, 148.92) * mm});
            skLineSegment(sketch, "E409", {"start": v(-283.05, 149.42) * mm, "end": v(-267.45, 149.42) * mm});
            skArc(sketch, "E410", {"start": v(-266.47, 148.92) * mm, "mid": v(-266.9, 149.29) * mm, "end": v(-267.45, 149.42) * mm});
            skLineSegment(sketch, "E411", {"start": v(-284.25, 161.22) * mm, "end": v(-284.25, 150.62) * mm});
            skArc(sketch, "E412", {"start": v(-284.25, 150.62) * mm, "mid": v(-283.9, 149.77) * mm, "end": v(-283.05, 149.42) * mm});
            skLineSegment(sketch, "E413", {"start": v(-276.25, 162.42) * mm, "end": v(-283.05, 162.42) * mm});
            skArc(sketch, "E414", {"start": v(-283.05, 162.42) * mm, "mid": v(-283.9, 162.07) * mm, "end": v(-284.25, 161.22) * mm});
            skLineSegment(sketch, "E415", {"start": v(-283.05, 166.92) * mm, "end": v(-276.25, 166.92) * mm});
            skArc(sketch, "E416", {"start": v(-276.25, 162.42) * mm, "mid": v(-274, 164.67) * mm, "end": v(-276.25, 166.92) * mm});
            skLineSegment(sketch, "E417", {"start": v(-284.25, 178.72) * mm, "end": v(-284.25, 168.12) * mm});
            skArc(sketch, "E418", {"start": v(-284.25, 168.12) * mm, "mid": v(-283.9, 167.27) * mm, "end": v(-283.05, 166.92) * mm});
            skLineSegment(sketch, "E419", {"start": v(-267.45, 179.92) * mm, "end": v(-283.05, 179.92) * mm});
            skArc(sketch, "E420", {"start": v(-283.05, 179.92) * mm, "mid": v(-283.9, 179.57) * mm, "end": v(-284.25, 178.72) * mm});
            skLineSegment(sketch, "E421", {"start": v(-128.25, 181.92) * mm, "end": v(-128.25, 182.72) * mm});
            skLineSegment(sketch, "E422", {"start": v(-266.25, 181.92) * mm, "end": v(-128.25, 181.92) * mm});
            skLineSegment(sketch, "E423", {"start": v(-266.25, 182.72) * mm, "end": v(-266.25, 181.92) * mm});
            skLineSegment(sketch, "E424", {"start": v(-129.45, 183.92) * mm, "end": v(-265.05, 183.92) * mm});
            skArc(sketch, "E425", {"start": v(-265.05, 183.92) * mm, "mid": v(-265.9, 183.57) * mm, "end": v(-266.25, 182.72) * mm});
            skArc(sketch, "E426", {"start": v(-128.25, 182.72) * mm, "mid": v(-128.6, 183.57) * mm, "end": v(-129.45, 183.92) * mm});
            skLineSegment(sketch, "E427", {"start": v(-128.25, 168.12) * mm, "end": v(-128.25, 182.72) * mm});
            skLineSegment(sketch, "E428", {"start": v(-266.25, 182.72) * mm, "end": v(-266.25, 181.12) * mm});
            skArc(sketch, "E429", {"start": v(-267.45, 179.92) * mm, "mid": v(-266.6, 180.27) * mm, "end": v(-266.25, 181.12) * mm});
            skLineSegment(sketch, "E430", {"start": v(-266.25, 148.22) * mm, "end": v(-266.25, 146.62) * mm});
            skArc(sketch, "E431", {"start": v(-266.25, 148.22) * mm, "mid": v(-266.6, 149.07) * mm, "end": v(-267.45, 149.42) * mm});
            skLineSegment(sketch, "E432", {"start": v(-265.05, 145.42) * mm, "end": v(-129.45, 145.42) * mm});
            skArc(sketch, "E433", {"start": v(-266.25, 146.62) * mm, "mid": v(-265.9, 145.77) * mm, "end": v(-265.05, 145.42) * mm});
            skLineSegment(sketch, "E434", {"start": v(-128.25, 146.62) * mm, "end": v(-128.25, 161.22) * mm});
            skArc(sketch, "E435", {"start": v(-129.45, 145.42) * mm, "mid": v(-128.6, 145.77) * mm, "end": v(-128.25, 146.62) * mm});
            skLineSegment(sketch, "E436", {"start": v(-266.25, 147.42) * mm, "end": v(-266.25, 146.62) * mm});
            skLineSegment(sketch, "E437", {"start": v(-128.25, 147.42) * mm, "end": v(-266.25, 147.42) * mm});
            skLineSegment(sketch, "E438", {"start": v(-128.25, 146.62) * mm, "end": v(-128.25, 147.42) * mm});
            skLineSegment(sketch, "E439", {"start": v(-128.25, 181.92) * mm, "end": v(-128.25, 180.42) * mm});
            skLineSegment(sketch, "E440", {"start": v(-266.25, 181.12) * mm, "end": v(-266.25, 181.92) * mm});
            skArc(sketch, "E441", {"start": v(-266.47, 180.42) * mm, "mid": v(-266.3, 180.75) * mm, "end": v(-266.25, 181.12) * mm});
            skArc(sketch, "E442", {"start": v(-266.25, 148.22) * mm, "mid": v(-266.3, 148.59) * mm, "end": v(-266.47, 148.92) * mm});
            skLineSegment(sketch, "E443", {"start": v(-266.25, 147.42) * mm, "end": v(-266.25, 148.22) * mm});
            skLineSegment(sketch, "E444", {"start": v(-128.25, 148.92) * mm, "end": v(-128.25, 147.42) * mm});
            skLineSegment(sketch, "E445", {"start": v(154.83, -63.83) * mm, "end": v(154.83, -61.83) * mm});
            skLineSegment(sketch, "E446", {"start": v(218.83, -63.83) * mm, "end": v(218.83, -61.83) * mm});
            skLineSegment(sketch, "E447", {"start": v(160.83, -55.83) * mm, "end": v(212.83, -55.83) * mm});
            skPoint(sketch, "E448.visualSharp", {"position": v(154.83, -55.83) * mm});
            skArc(sketch, "E448.filletArc", {"start": v(160.83, -55.83) * mm, "mid": v(156.6, -57.58) * mm, "end": v(154.83, -61.83) * mm});
            skPoint(sketch, "E449.visualSharp", {"position": v(218.83, -55.83) * mm});
            skArc(sketch, "E449.filletArc", {"start": v(218.83, -61.83) * mm, "mid": v(217.08, -57.58) * mm, "end": v(212.83, -55.83) * mm});
            skSolve(sketch);
        }
        {
            var Q0;
            Q0 = qSketchRegion(id + "F0", true);
            extrude(context, id + "F1", {"entities" : qUnion([Q0]), "depth" : 1.5 * mm});
        }
        {
            var Q0;
            Q0=makeQuery(id+"F1.opExtrude","CAP_FACE",FACE,{"disambiguationData":[OSD([sQuery(id+"F0.wireOp",EDGE,"E119"),sQuery(id+"F0.wireOp",EDGE,"E121"),sQuery(id+"F0.wireOp",EDGE,"E120"),sQuery(id+"F0.wireOp",EDGE,"E123"),sQuery(id+"F0.wireOp",EDGE,"E122"),sQuery(id+"F0.wireOp",EDGE,"E124"),sQuery(id+"F0.wireOp",EDGE,"E125"),sQuery(id+"F0.wireOp",EDGE,"E128"),sQuery(id+"F0.wireOp",EDGE,"E127"),sQuery(id+"F0.wireOp",EDGE,"E126"),sQuery(id+"F0.wireOp",EDGE,"E129"),sQuery(id+"F0.wireOp",EDGE,"E131"),sQuery(id+"F0.wireOp",EDGE,"E130"),sQuery(id+"F0.wireOp",EDGE,"E188"),sQuery(id+"F0.wireOp",EDGE,"E190"),sQuery(id+"F0.wireOp",EDGE,"E186"),sQuery(id+"F0.wireOp",EDGE,"E189"),sQuery(id+"F0.wireOp",EDGE,"E185"),sQuery(id+"F0.wireOp",EDGE,"E187"),sQuery(id+"F0.wireOp",EDGE,"E184"),sQuery(id+"F0.wireOp",EDGE,"E182"),sQuery(id+"F0.wireOp",EDGE,"E180"),sQuery(id+"F0.wireOp",EDGE,"E183"),sQuery(id+"F0.wireOp",EDGE,"E179"),sQuery(id+"F0.wireOp",EDGE,"E181"),sQuery(id+"F0.wireOp",EDGE,"E177"),sQuery(id+"F0.wireOp",EDGE,"E178"),sQuery(id+"F0.wireOp",EDGE,"E174"),sQuery(id+"F0.wireOp",EDGE,"E176"),sQuery(id+"F0.wireOp",EDGE,"E172"),sQuery(id+"F0.wireOp",EDGE,"E175"),sQuery(id+"F0.wireOp",EDGE,"E170"),sQuery(id+"F0.wireOp",EDGE,"E173"),sQuery(id+"F0.wireOp",EDGE,"E168"),sQuery(id+"F0.wireOp",EDGE,"E171"),sQuery(id+"F0.wireOp",EDGE,"E166"),sQuery(id+"F0.wireOp",EDGE,"E169"),sQuery(id+"F0.wireOp",EDGE,"E164"),sQuery(id+"F0.wireOp",EDGE,"E167"),sQuery(id+"F0.wireOp",EDGE,"E162"),sQuery(id+"F0.wireOp",EDGE,"E165"),sQuery(id+"F0.wireOp",EDGE,"E160"),sQuery(id+"F0.wireOp",EDGE,"E163"),sQuery(id+"F0.wireOp",EDGE,"E158"),sQuery(id+"F0.wireOp",EDGE,"E161"),sQuery(id+"F0.wireOp",EDGE,"E156"),sQuery(id+"F0.wireOp",EDGE,"E159"),sQuery(id+"F0.wireOp",EDGE,"E154"),sQuery(id+"F0.wireOp",EDGE,"E157"),sQuery(id+"F0.wireOp",EDGE,"E152"),sQuery(id+"F0.wireOp",EDGE,"E155"),sQuery(id+"F0.wireOp",EDGE,"E150"),sQuery(id+"F0.wireOp",EDGE,"E153"),sQuery(id+"F0.wireOp",EDGE,"E148"),sQuery(id+"F0.wireOp",EDGE,"E151"),sQuery(id+"F0.wireOp",EDGE,"E146"),sQuery(id+"F0.wireOp",EDGE,"E149"),sQuery(id+"F0.wireOp",EDGE,"E147"),sQuery(id+"F0.wireOp",EDGE,"E144"),sQuery(id+"F0.wireOp",EDGE,"E145"),sQuery(id+"F0.wireOp",EDGE,"E142"),sQuery(id+"F0.wireOp",EDGE,"E140"),sQuery(id+"F0.wireOp",EDGE,"E143"),sQuery(id+"F0.wireOp",EDGE,"E139"),sQuery(id+"F0.wireOp",EDGE,"E141"),sQuery(id+"F0.wireOp",EDGE,"E138"),sQuery(id+"F0.wireOp",EDGE,"E136"),sQuery(id+"F0.wireOp",EDGE,"E134"),sQuery(id+"F0.wireOp",EDGE,"E137"),sQuery(id+"F0.wireOp",EDGE,"E132"),sQuery(id+"F0.wireOp",EDGE,"E135"),sQuery(id+"F0.wireOp",EDGE,"E133"),sQuery(id+"F0.wireOp",EDGE,"E191"),sQuery(id+"F0.wireOp",EDGE,"E192"),sQuery(id+"F0.wireOp",EDGE,"E193"),sQuery(id+"F0.wireOp",EDGE,"E194"),sQuery(id+"F0.wireOp",EDGE,"E195"),sQuery(id+"F0.wireOp",EDGE,"E196"),sQuery(id+"F0.wireOp",EDGE,"E220"),sQuery(id+"F0.wireOp",EDGE,"E213"),sQuery(id+"F0.wireOp",EDGE,"E215"),sQuery(id+"F0.wireOp",EDGE,"E214"),sQuery(id+"F0.wireOp",EDGE,"E217"),sQuery(id+"F0.wireOp",EDGE,"E216"),sQuery(id+"F0.wireOp",EDGE,"E219"),sQuery(id+"F0.wireOp",EDGE,"E218"),sQuery(id+"F0.wireOp",EDGE,"E212"),sQuery(id+"F0.wireOp",EDGE,"E211"),sQuery(id+"F0.wireOp",EDGE,"E205"),sQuery(id+"F0.wireOp",EDGE,"E206"),sQuery(id+"F0.wireOp",EDGE,"E208"),sQuery(id+"F0.wireOp",EDGE,"E207"),sQuery(id+"F0.wireOp",EDGE,"E210"),sQuery(id+"F0.wireOp",EDGE,"E209"),sQuery(id+"F0.wireOp",EDGE,"E199"),sQuery(id+"F0.wireOp",EDGE,"E198"),sQuery(id+"F0.wireOp",EDGE,"E201"),sQuery(id+"F0.wireOp",EDGE,"E200"),sQuery(id+"F0.wireOp",EDGE,"E203"),sQuery(id+"F0.wireOp",EDGE,"E202"),sQuery(id+"F0.wireOp",EDGE,"E204"),sQuery(id+"F0.wireOp",EDGE,"E197")])],"isStart":false});
            var sketch = newSketch(context, id + "F2", { "sketchPlane" : qUnion([Q0])});
            skLineSegment(sketch, "E450.bottom", {"start": v(-13.67, 14.34) * mm, "end": v(20.33, 14.34) * mm});
            skLineSegment(sketch, "E450.top", {"start": v(-13.67, -21.66) * mm, "end": v(20.33, -21.66) * mm});
            skLineSegment(sketch, "E450.left", {"start": v(-14.67, 13.34) * mm, "end": v(-14.67, -20.66) * mm});
            skLineSegment(sketch, "E450.right", {"start": v(21.33, 13.34) * mm, "end": v(21.33, -20.66) * mm});
            skPoint(sketch, "E451.visualSharp", {"position": v(-14.67, 14.34) * mm});
            skArc(sketch, "E451.filletArc", {"start": v(-13.67, 14.34) * mm, "mid": v(-14.38, 14.05) * mm, "end": v(-14.67, 13.34) * mm});
            skPoint(sketch, "E452.visualSharp", {"position": v(21.33, 14.34) * mm});
            skArc(sketch, "E452.filletArc", {"start": v(21.33, 13.34) * mm, "mid": v(21.03, 14.05) * mm, "end": v(20.33, 14.34) * mm});
            skPoint(sketch, "E453.visualSharp", {"position": v(21.33, -21.66) * mm});
            skArc(sketch, "E453.filletArc", {"start": v(20.33, -21.66) * mm, "mid": v(21.03, -21.37) * mm, "end": v(21.33, -20.66) * mm});
            skPoint(sketch, "E454.visualSharp", {"position": v(-14.67, -21.66) * mm});
            skArc(sketch, "E454.filletArc", {"start": v(-14.67, -20.66) * mm, "mid": v(-14.38, -21.37) * mm, "end": v(-13.67, -21.66) * mm});
            skLineSegment(sketch, "E455.bottom", {"start": v(-18.51, 18.2) * mm, "end": v(25.71, 18.2) * mm});
            skLineSegment(sketch, "E455.top", {"start": v(-18.51, -25.95) * mm, "end": v(25.71, -25.95) * mm});
            skLineSegment(sketch, "E455.left", {"start": v(-18.51, 18.2) * mm, "end": v(-18.51, -25.95) * mm});
            skLineSegment(sketch, "E455.right", {"start": v(25.71, 18.2) * mm, "end": v(25.71, -25.95) * mm});
            skSolve(sketch);
        }
        {
            var Q0;
            Q0 = qSketchRegion(id + "F2", true);
            extrude(context, id + "F3", {"entities" : qUnion([Q0]), "operationType" : NewBodyOperationType.ADD, "oppositeDirection" : true, "depth" : 0.7 * mm});
        }
        {
            var Q0;
            Q0=makeQuery(id+"F3.boolean.opBoolean","MERGE",FACE,{"derivedFrom":[makeQuery(id+"F1.opExtrude","CAP_FACE",FACE,{"disambiguationData":[OSD([sQuery(id+"F0.wireOp",EDGE,"E119"),sQuery(id+"F0.wireOp",EDGE,"E121"),sQuery(id+"F0.wireOp",EDGE,"E120"),sQuery(id+"F0.wireOp",EDGE,"E123"),sQuery(id+"F0.wireOp",EDGE,"E122"),sQuery(id+"F0.wireOp",EDGE,"E124"),sQuery(id+"F0.wireOp",EDGE,"E125"),sQuery(id+"F0.wireOp",EDGE,"E128"),sQuery(id+"F0.wireOp",EDGE,"E127"),sQuery(id+"F0.wireOp",EDGE,"E126"),sQuery(id+"F0.wireOp",EDGE,"E129"),sQuery(id+"F0.wireOp",EDGE,"E131"),sQuery(id+"F0.wireOp",EDGE,"E130"),sQuery(id+"F0.wireOp",EDGE,"E188"),sQuery(id+"F0.wireOp",EDGE,"E190"),sQuery(id+"F0.wireOp",EDGE,"E186"),sQuery(id+"F0.wireOp",EDGE,"E189"),sQuery(id+"F0.wireOp",EDGE,"E185"),sQuery(id+"F0.wireOp",EDGE,"E187"),sQuery(id+"F0.wireOp",EDGE,"E184"),sQuery(id+"F0.wireOp",EDGE,"E182"),sQuery(id+"F0.wireOp",EDGE,"E180"),sQuery(id+"F0.wireOp",EDGE,"E183"),sQuery(id+"F0.wireOp",EDGE,"E179"),sQuery(id+"F0.wireOp",EDGE,"E181"),sQuery(id+"F0.wireOp",EDGE,"E177"),sQuery(id+"F0.wireOp",EDGE,"E178"),sQuery(id+"F0.wireOp",EDGE,"E174"),sQuery(id+"F0.wireOp",EDGE,"E176"),sQuery(id+"F0.wireOp",EDGE,"E172"),sQuery(id+"F0.wireOp",EDGE,"E175"),sQuery(id+"F0.wireOp",EDGE,"E170"),sQuery(id+"F0.wireOp",EDGE,"E173"),sQuery(id+"F0.wireOp",EDGE,"E168"),sQuery(id+"F0.wireOp",EDGE,"E171"),sQuery(id+"F0.wireOp",EDGE,"E166"),sQuery(id+"F0.wireOp",EDGE,"E169"),sQuery(id+"F0.wireOp",EDGE,"E164"),sQuery(id+"F0.wireOp",EDGE,"E167"),sQuery(id+"F0.wireOp",EDGE,"E162"),sQuery(id+"F0.wireOp",EDGE,"E165"),sQuery(id+"F0.wireOp",EDGE,"E160"),sQuery(id+"F0.wireOp",EDGE,"E163"),sQuery(id+"F0.wireOp",EDGE,"E158"),sQuery(id+"F0.wireOp",EDGE,"E161"),sQuery(id+"F0.wireOp",EDGE,"E156"),sQuery(id+"F0.wireOp",EDGE,"E159"),sQuery(id+"F0.wireOp",EDGE,"E154"),sQuery(id+"F0.wireOp",EDGE,"E157"),sQuery(id+"F0.wireOp",EDGE,"E152"),sQuery(id+"F0.wireOp",EDGE,"E155"),sQuery(id+"F0.wireOp",EDGE,"E150"),sQuery(id+"F0.wireOp",EDGE,"E153"),sQuery(id+"F0.wireOp",EDGE,"E148"),sQuery(id+"F0.wireOp",EDGE,"E151"),sQuery(id+"F0.wireOp",EDGE,"E146"),sQuery(id+"F0.wireOp",EDGE,"E149"),sQuery(id+"F0.wireOp",EDGE,"E147"),sQuery(id+"F0.wireOp",EDGE,"E144"),sQuery(id+"F0.wireOp",EDGE,"E145"),sQuery(id+"F0.wireOp",EDGE,"E142"),sQuery(id+"F0.wireOp",EDGE,"E140"),sQuery(id+"F0.wireOp",EDGE,"E143"),sQuery(id+"F0.wireOp",EDGE,"E139"),sQuery(id+"F0.wireOp",EDGE,"E141"),sQuery(id+"F0.wireOp",EDGE,"E138"),sQuery(id+"F0.wireOp",EDGE,"E136"),sQuery(id+"F0.wireOp",EDGE,"E134"),sQuery(id+"F0.wireOp",EDGE,"E137"),sQuery(id+"F0.wireOp",EDGE,"E132"),sQuery(id+"F0.wireOp",EDGE,"E135"),sQuery(id+"F0.wireOp",EDGE,"E133"),sQuery(id+"F0.wireOp",EDGE,"E191"),sQuery(id+"F0.wireOp",EDGE,"E192"),sQuery(id+"F0.wireOp",EDGE,"E193"),sQuery(id+"F0.wireOp",EDGE,"E194"),sQuery(id+"F0.wireOp",EDGE,"E195"),sQuery(id+"F0.wireOp",EDGE,"E196"),sQuery(id+"F0.wireOp",EDGE,"E220"),sQuery(id+"F0.wireOp",EDGE,"E213"),sQuery(id+"F0.wireOp",EDGE,"E215"),sQuery(id+"F0.wireOp",EDGE,"E214"),sQuery(id+"F0.wireOp",EDGE,"E217"),sQuery(id+"F0.wireOp",EDGE,"E216"),sQuery(id+"F0.wireOp",EDGE,"E219"),sQuery(id+"F0.wireOp",EDGE,"E218"),sQuery(id+"F0.wireOp",EDGE,"E212"),sQuery(id+"F0.wireOp",EDGE,"E211"),sQuery(id+"F0.wireOp",EDGE,"E205"),sQuery(id+"F0.wireOp",EDGE,"E206"),sQuery(id+"F0.wireOp",EDGE,"E208"),sQuery(id+"F0.wireOp",EDGE,"E207"),sQuery(id+"F0.wireOp",EDGE,"E210"),sQuery(id+"F0.wireOp",EDGE,"E209"),sQuery(id+"F0.wireOp",EDGE,"E199"),sQuery(id+"F0.wireOp",EDGE,"E198"),sQuery(id+"F0.wireOp",EDGE,"E201"),sQuery(id+"F0.wireOp",EDGE,"E200"),sQuery(id+"F0.wireOp",EDGE,"E203"),sQuery(id+"F0.wireOp",EDGE,"E202"),sQuery(id+"F0.wireOp",EDGE,"E204"),sQuery(id+"F0.wireOp",EDGE,"E197")])],"isStart":false}),makeQuery(id+"F3.opExtrude","CAP_FACE",FACE,{"disambiguationData":[OSD([sQuery(id+"F2.wireOp",EDGE,"E450.bottom"),sQuery(id+"F2.wireOp",EDGE,"E450.top"),sQuery(id+"F2.wireOp",EDGE,"E450.left"),sQuery(id+"F2.wireOp",EDGE,"E450.right"),sQuery(id+"F2.wireOp",EDGE,"E451.filletArc"),sQuery(id+"F2.wireOp",EDGE,"E452.filletArc"),sQuery(id+"F2.wireOp",EDGE,"E453.filletArc"),sQuery(id+"F2.wireOp",EDGE,"E454.filletArc"),sQuery(id+"F2.wireOp",EDGE,"E455.bottom"),sQuery(id+"F2.wireOp",EDGE,"E455.top"),sQuery(id+"F2.wireOp",EDGE,"E455.left"),sQuery(id+"F2.wireOp",EDGE,"E455.right")])],"isStart":true})]});
            var sketch = newSketch(context, id + "F4", { "sketchPlane" : qUnion([Q0])});
            skLineSegment(sketch, "E456.bottom", {"start": v(-13.67, 123.34) * mm, "end": v(20.33, 123.34) * mm});
            skLineSegment(sketch, "E456.top", {"start": v(-13.67, 26.34) * mm, "end": v(20.33, 26.34) * mm});
            skLineSegment(sketch, "E456.left", {"start": v(-14.67, 122.34) * mm, "end": v(-14.67, 27.34) * mm});
            skLineSegment(sketch, "E456.right", {"start": v(21.33, 122.34) * mm, "end": v(21.33, 27.34) * mm});
            skLineSegment(sketch, "E457.bottom", {"start": v(-7.67, 171.34) * mm, "end": v(14.33, 171.34) * mm});
            skLineSegment(sketch, "E457.top", {"start": v(-7.67, 133.34) * mm, "end": v(14.33, 133.34) * mm});
            skLineSegment(sketch, "E457.left", {"start": v(-8.67, 170.34) * mm, "end": v(-8.67, 134.34) * mm});
            skLineSegment(sketch, "E457.right", {"start": v(15.33, 170.34) * mm, "end": v(15.33, 134.34) * mm});
            skPoint(sketch, "E458.visualSharp", {"position": v(-8.67, 171.34) * mm});
            skArc(sketch, "E458.filletArc", {"start": v(-7.67, 171.34) * mm, "mid": v(-8.38, 171.05) * mm, "end": v(-8.67, 170.34) * mm});
            skPoint(sketch, "E459.visualSharp", {"position": v(15.33, 171.34) * mm});
            skArc(sketch, "E459.filletArc", {"start": v(15.33, 170.34) * mm, "mid": v(15.03, 171.05) * mm, "end": v(14.33, 171.34) * mm});
            skPoint(sketch, "E460.visualSharp", {"position": v(15.33, 133.34) * mm});
            skArc(sketch, "E460.filletArc", {"start": v(14.33, 133.34) * mm, "mid": v(15.03, 133.63) * mm, "end": v(15.33, 134.34) * mm});
            skPoint(sketch, "E461.visualSharp", {"position": v(-8.67, 133.34) * mm});
            skArc(sketch, "E461.filletArc", {"start": v(-8.67, 134.34) * mm, "mid": v(-8.38, 133.63) * mm, "end": v(-7.67, 133.34) * mm});
            skPoint(sketch, "E462.visualSharp", {"position": v(-14.67, 123.34) * mm});
            skArc(sketch, "E462.filletArc", {"start": v(-13.67, 123.34) * mm, "mid": v(-14.38, 123.05) * mm, "end": v(-14.67, 122.34) * mm});
            skPoint(sketch, "E463.visualSharp", {"position": v(21.33, 123.34) * mm});
            skArc(sketch, "E463.filletArc", {"start": v(21.33, 122.34) * mm, "mid": v(21.03, 123.05) * mm, "end": v(20.33, 123.34) * mm});
            skPoint(sketch, "E464.visualSharp", {"position": v(21.33, 26.34) * mm});
            skArc(sketch, "E464.filletArc", {"start": v(20.33, 26.34) * mm, "mid": v(21.03, 26.63) * mm, "end": v(21.33, 27.34) * mm});
            skPoint(sketch, "E465.visualSharp", {"position": v(-14.67, 26.34) * mm});
            skArc(sketch, "E465.filletArc", {"start": v(-14.67, 27.34) * mm, "mid": v(-14.38, 26.63) * mm, "end": v(-13.67, 26.34) * mm});
            skLineSegment(sketch, "E466.bottom", {"start": v(-19.64, 128.29) * mm, "end": v(25.24, 128.29) * mm});
            skLineSegment(sketch, "E466.top", {"start": v(-19.64, 22.26) * mm, "end": v(25.24, 22.26) * mm});
            skLineSegment(sketch, "E466.left", {"start": v(-19.64, 128.29) * mm, "end": v(-19.64, 22.26) * mm});
            skLineSegment(sketch, "E466.right", {"start": v(25.24, 128.29) * mm, "end": v(25.24, 22.26) * mm});
            skLineSegment(sketch, "E467.bottom", {"start": v(-13.67, 176.27) * mm, "end": v(19.52, 176.27) * mm});
            skLineSegment(sketch, "E467.top", {"start": v(-13.67, 128.29) * mm, "end": v(19.52, 128.29) * mm});
            skLineSegment(sketch, "E467.left", {"start": v(-13.67, 176.27) * mm, "end": v(-13.67, 128.29) * mm});
            skLineSegment(sketch, "E467.right", {"start": v(19.52, 176.27) * mm, "end": v(19.52, 128.29) * mm});
            skSolve(sketch);
        }
        {
            var Q0;
            Q0 = qSketchRegion(id + "F4", true);
            extrude(context, id + "F5", {"entities" : qUnion([Q0]), "operationType" : NewBodyOperationType.ADD, "oppositeDirection" : true, "depth" : 0.7 * mm});
        }
        {
            var Q0;
            Q0=makeQuery(id+"F1.opExtrude","CAP_FACE",FACE,{"disambiguationData":[OSD([sQuery(id+"F0.wireOp",EDGE,"E221"),sQuery(id+"F0.wireOp",EDGE,"E223"),sQuery(id+"F0.wireOp",EDGE,"E222"),sQuery(id+"F0.wireOp",EDGE,"E225"),sQuery(id+"F0.wireOp",EDGE,"E232"),sQuery(id+"F0.wireOp",EDGE,"E235"),sQuery(id+"F0.wireOp",EDGE,"E257"),sQuery(id+"F0.wireOp",EDGE,"E233"),sQuery(id+"F0.wireOp",EDGE,"E254"),sQuery(id+"F0.wireOp",EDGE,"E256"),sQuery(id+"F0.wireOp",EDGE,"E258"),sQuery(id+"F0.wireOp",EDGE,"E255"),sQuery(id+"F0.wireOp",EDGE,"E249"),sQuery(id+"F0.wireOp",EDGE,"E259"),sQuery(id+"F0.wireOp",EDGE,"E247"),sQuery(id+"F0.wireOp",EDGE,"E250"),sQuery(id+"F0.wireOp",EDGE,"E245"),sQuery(id+"F0.wireOp",EDGE,"E248"),sQuery(id+"F0.wireOp",EDGE,"E243"),sQuery(id+"F0.wireOp",EDGE,"E246"),sQuery(id+"F0.wireOp",EDGE,"E241"),sQuery(id+"F0.wireOp",EDGE,"E244"),sQuery(id+"F0.wireOp",EDGE,"E239"),sQuery(id+"F0.wireOp",EDGE,"E242"),sQuery(id+"F0.wireOp",EDGE,"E261"),sQuery(id+"F0.wireOp",EDGE,"E264"),sQuery(id+"F0.wireOp",EDGE,"E234"),sQuery(id+"F0.wireOp",EDGE,"E237"),sQuery(id+"F0.wireOp",EDGE,"E224"),sQuery(id+"F0.wireOp",EDGE,"E227"),sQuery(id+"F0.wireOp",EDGE,"E226"),sQuery(id+"F0.wireOp",EDGE,"E228"),sQuery(id+"F0.wireOp",EDGE,"E266"),sQuery(id+"F0.wireOp",EDGE,"E268"),sQuery(id+"F0.wireOp",EDGE,"E262"),sQuery(id+"F0.wireOp",EDGE,"E265"),sQuery(id+"F0.wireOp",EDGE,"E263"),sQuery(id+"F0.wireOp",EDGE,"E269"),sQuery(id+"F0.wireOp",EDGE,"E270"),sQuery(id+"F0.wireOp",EDGE,"E271"),sQuery(id+"F0.wireOp",EDGE,"E272"),sQuery(id+"F0.wireOp",EDGE,"E273"),sQuery(id+"F0.wireOp",EDGE,"E274")])],"isStart":false});
            var sketch = newSketch(context, id + "F6", { "sketchPlane" : qUnion([Q0])});
            skLineSegment(sketch, "E468.bottom", {"start": v(-30.03, -148.63) * mm, "end": v(125.97, -148.63) * mm});
            skLineSegment(sketch, "E468.top", {"start": v(-30.03, -150.15) * mm, "end": v(125.97, -150.15) * mm});
            skLineSegment(sketch, "E468.left", {"start": v(-30.03, -148.63) * mm, "end": v(-30.03, -150.15) * mm});
            skLineSegment(sketch, "E468.right", {"start": v(125.97, -148.63) * mm, "end": v(125.97, -150.15) * mm});
            skLineSegment(sketch, "E469.bottom", {"start": v(-24.96, -117.05) * mm, "end": v(119.9, -117.05) * mm});
            skLineSegment(sketch, "E469.top", {"start": v(-24.96, -115.53) * mm, "end": v(119.9, -115.53) * mm});
            skLineSegment(sketch, "E469.left", {"start": v(-24.96, -117.05) * mm, "end": v(-24.96, -115.53) * mm});
            skLineSegment(sketch, "E469.right", {"start": v(119.9, -117.05) * mm, "end": v(119.9, -115.53) * mm});
            skSolve(sketch);
        }
        {
            var Q0;
            Q0 = qSketchRegion(id + "F6", true);
            extrude(context, id + "F7", {"entities" : qUnion([Q0]), "operationType" : NewBodyOperationType.REMOVE, "oppositeDirection" : true, "depth" : 0.7 * mm});
        }
        {
            var Q0;
            Q0=makeQuery(id+"F1.opExtrude","SWEPT_BODY",BODY,{"disambiguationData":[OSD([sQuery(id+"F0.wireOp",EDGE,"E391"),sQuery(id+"F0.wireOp",EDGE,"E393"),sQuery(id+"F0.wireOp",EDGE,"E392"),sQuery(id+"F0.wireOp",EDGE,"E395"),sQuery(id+"F0.wireOp",EDGE,"E402"),sQuery(id+"F0.wireOp",EDGE,"E405"),sQuery(id+"F0.wireOp",EDGE,"E427"),sQuery(id+"F0.wireOp",EDGE,"E403"),sQuery(id+"F0.wireOp",EDGE,"E424"),sQuery(id+"F0.wireOp",EDGE,"E426"),sQuery(id+"F0.wireOp",EDGE,"E428"),sQuery(id+"F0.wireOp",EDGE,"E425"),sQuery(id+"F0.wireOp",EDGE,"E419"),sQuery(id+"F0.wireOp",EDGE,"E429"),sQuery(id+"F0.wireOp",EDGE,"E417"),sQuery(id+"F0.wireOp",EDGE,"E420"),sQuery(id+"F0.wireOp",EDGE,"E415"),sQuery(id+"F0.wireOp",EDGE,"E418"),sQuery(id+"F0.wireOp",EDGE,"E413"),sQuery(id+"F0.wireOp",EDGE,"E416"),sQuery(id+"F0.wireOp",EDGE,"E411"),sQuery(id+"F0.wireOp",EDGE,"E414"),sQuery(id+"F0.wireOp",EDGE,"E409"),sQuery(id+"F0.wireOp",EDGE,"E412"),sQuery(id+"F0.wireOp",EDGE,"E431"),sQuery(id+"F0.wireOp",EDGE,"E434"),sQuery(id+"F0.wireOp",EDGE,"E404"),sQuery(id+"F0.wireOp",EDGE,"E407"),sQuery(id+"F0.wireOp",EDGE,"E394"),sQuery(id+"F0.wireOp",EDGE,"E397"),sQuery(id+"F0.wireOp",EDGE,"E396"),sQuery(id+"F0.wireOp",EDGE,"E398"),sQuery(id+"F0.wireOp",EDGE,"E436"),sQuery(id+"F0.wireOp",EDGE,"E438"),sQuery(id+"F0.wireOp",EDGE,"E432"),sQuery(id+"F0.wireOp",EDGE,"E435"),sQuery(id+"F0.wireOp",EDGE,"E433"),sQuery(id+"F0.wireOp",EDGE,"E439"),sQuery(id+"F0.wireOp",EDGE,"E440"),sQuery(id+"F0.wireOp",EDGE,"E441"),sQuery(id+"F0.wireOp",EDGE,"E442"),sQuery(id+"F0.wireOp",EDGE,"E443"),sQuery(id+"F0.wireOp",EDGE,"E444")])]});
            deleteBodies(context, id + "F8", {"entities" : qUnion([Q0])});
        }
        {
            var Q0;
            Q0=makeQuery(id+"F1.opExtrude","SWEPT_BODY",BODY,{"disambiguationData":[OSD([sQuery(id+"F0.wireOp",EDGE,"E119"),sQuery(id+"F0.wireOp",EDGE,"E121"),sQuery(id+"F0.wireOp",EDGE,"E120"),sQuery(id+"F0.wireOp",EDGE,"E123"),sQuery(id+"F0.wireOp",EDGE,"E122"),sQuery(id+"F0.wireOp",EDGE,"E124"),sQuery(id+"F0.wireOp",EDGE,"E125"),sQuery(id+"F0.wireOp",EDGE,"E128"),sQuery(id+"F0.wireOp",EDGE,"E127"),sQuery(id+"F0.wireOp",EDGE,"E126"),sQuery(id+"F0.wireOp",EDGE,"E129"),sQuery(id+"F0.wireOp",EDGE,"E131"),sQuery(id+"F0.wireOp",EDGE,"E130"),sQuery(id+"F0.wireOp",EDGE,"E188"),sQuery(id+"F0.wireOp",EDGE,"E190"),sQuery(id+"F0.wireOp",EDGE,"E186"),sQuery(id+"F0.wireOp",EDGE,"E189"),sQuery(id+"F0.wireOp",EDGE,"E185"),sQuery(id+"F0.wireOp",EDGE,"E187"),sQuery(id+"F0.wireOp",EDGE,"E184"),sQuery(id+"F0.wireOp",EDGE,"E182"),sQuery(id+"F0.wireOp",EDGE,"E180"),sQuery(id+"F0.wireOp",EDGE,"E183"),sQuery(id+"F0.wireOp",EDGE,"E179"),sQuery(id+"F0.wireOp",EDGE,"E181"),sQuery(id+"F0.wireOp",EDGE,"E177"),sQuery(id+"F0.wireOp",EDGE,"E178"),sQuery(id+"F0.wireOp",EDGE,"E174"),sQuery(id+"F0.wireOp",EDGE,"E176"),sQuery(id+"F0.wireOp",EDGE,"E172"),sQuery(id+"F0.wireOp",EDGE,"E175"),sQuery(id+"F0.wireOp",EDGE,"E170"),sQuery(id+"F0.wireOp",EDGE,"E173"),sQuery(id+"F0.wireOp",EDGE,"E168"),sQuery(id+"F0.wireOp",EDGE,"E171"),sQuery(id+"F0.wireOp",EDGE,"E166"),sQuery(id+"F0.wireOp",EDGE,"E169"),sQuery(id+"F0.wireOp",EDGE,"E164"),sQuery(id+"F0.wireOp",EDGE,"E167"),sQuery(id+"F0.wireOp",EDGE,"E162"),sQuery(id+"F0.wireOp",EDGE,"E165"),sQuery(id+"F0.wireOp",EDGE,"E160"),sQuery(id+"F0.wireOp",EDGE,"E163"),sQuery(id+"F0.wireOp",EDGE,"E158"),sQuery(id+"F0.wireOp",EDGE,"E161"),sQuery(id+"F0.wireOp",EDGE,"E156"),sQuery(id+"F0.wireOp",EDGE,"E159"),sQuery(id+"F0.wireOp",EDGE,"E154"),sQuery(id+"F0.wireOp",EDGE,"E157"),sQuery(id+"F0.wireOp",EDGE,"E152"),sQuery(id+"F0.wireOp",EDGE,"E155"),sQuery(id+"F0.wireOp",EDGE,"E150"),sQuery(id+"F0.wireOp",EDGE,"E153"),sQuery(id+"F0.wireOp",EDGE,"E148"),sQuery(id+"F0.wireOp",EDGE,"E151"),sQuery(id+"F0.wireOp",EDGE,"E146"),sQuery(id+"F0.wireOp",EDGE,"E149"),sQuery(id+"F0.wireOp",EDGE,"E147"),sQuery(id+"F0.wireOp",EDGE,"E144"),sQuery(id+"F0.wireOp",EDGE,"E145"),sQuery(id+"F0.wireOp",EDGE,"E142"),sQuery(id+"F0.wireOp",EDGE,"E140"),sQuery(id+"F0.wireOp",EDGE,"E143"),sQuery(id+"F0.wireOp",EDGE,"E139"),sQuery(id+"F0.wireOp",EDGE,"E141"),sQuery(id+"F0.wireOp",EDGE,"E138"),sQuery(id+"F0.wireOp",EDGE,"E136"),sQuery(id+"F0.wireOp",EDGE,"E134"),sQuery(id+"F0.wireOp",EDGE,"E137"),sQuery(id+"F0.wireOp",EDGE,"E132"),sQuery(id+"F0.wireOp",EDGE,"E135"),sQuery(id+"F0.wireOp",EDGE,"E133"),sQuery(id+"F0.wireOp",EDGE,"E191"),sQuery(id+"F0.wireOp",EDGE,"E192"),sQuery(id+"F0.wireOp",EDGE,"E193"),sQuery(id+"F0.wireOp",EDGE,"E194"),sQuery(id+"F0.wireOp",EDGE,"E195"),sQuery(id+"F0.wireOp",EDGE,"E196"),sQuery(id+"F0.wireOp",EDGE,"E220"),sQuery(id+"F0.wireOp",EDGE,"E213"),sQuery(id+"F0.wireOp",EDGE,"E215"),sQuery(id+"F0.wireOp",EDGE,"E214"),sQuery(id+"F0.wireOp",EDGE,"E217"),sQuery(id+"F0.wireOp",EDGE,"E216"),sQuery(id+"F0.wireOp",EDGE,"E219"),sQuery(id+"F0.wireOp",EDGE,"E218"),sQuery(id+"F0.wireOp",EDGE,"E212"),sQuery(id+"F0.wireOp",EDGE,"E211"),sQuery(id+"F0.wireOp",EDGE,"E205"),sQuery(id+"F0.wireOp",EDGE,"E206"),sQuery(id+"F0.wireOp",EDGE,"E208"),sQuery(id+"F0.wireOp",EDGE,"E207"),sQuery(id+"F0.wireOp",EDGE,"E210"),sQuery(id+"F0.wireOp",EDGE,"E209"),sQuery(id+"F0.wireOp",EDGE,"E199"),sQuery(id+"F0.wireOp",EDGE,"E198"),sQuery(id+"F0.wireOp",EDGE,"E201"),sQuery(id+"F0.wireOp",EDGE,"E200"),sQuery(id+"F0.wireOp",EDGE,"E203"),sQuery(id+"F0.wireOp",EDGE,"E202"),sQuery(id+"F0.wireOp",EDGE,"E204"),sQuery(id+"F0.wireOp",EDGE,"E197")])]});
            transform(context, id + "F9", {"entities" : qUnion([Q0]), "transformType" : TransformType.TRANSLATION_3D, "dx" : -200 * mm, "dy" : 75 * mm, "dz" : 0 * mm, "makeCopy" : false});
        }
        {
            var Q0;
            Q0=makeQuery(id+"F1.opExtrude","SWEPT_BODY",BODY,{"disambiguationData":[OSD([sQuery(id+"F0.wireOp",EDGE,"E275"),sQuery(id+"F0.wireOp",EDGE,"E276"),sQuery(id+"F0.wireOp",EDGE,"E277"),sQuery(id+"F0.wireOp",EDGE,"E278"),sQuery(id+"F0.wireOp",EDGE,"E279"),sQuery(id+"F0.wireOp",EDGE,"E280"),sQuery(id+"F0.wireOp",EDGE,"E281"),sQuery(id+"F0.wireOp",EDGE,"E282"),sQuery(id+"F0.wireOp",EDGE,"E283"),sQuery(id+"F0.wireOp",EDGE,"E284"),sQuery(id+"F0.wireOp",EDGE,"E285"),sQuery(id+"F0.wireOp",EDGE,"E286"),sQuery(id+"F0.wireOp",EDGE,"E287"),sQuery(id+"F0.wireOp",EDGE,"E288"),sQuery(id+"F0.wireOp",EDGE,"E289"),sQuery(id+"F0.wireOp",EDGE,"E290"),sQuery(id+"F0.wireOp",EDGE,"E291"),sQuery(id+"F0.wireOp",EDGE,"E292"),sQuery(id+"F0.wireOp",EDGE,"E293"),sQuery(id+"F0.wireOp",EDGE,"E294"),sQuery(id+"F0.wireOp",EDGE,"E295"),sQuery(id+"F0.wireOp",EDGE,"E296"),sQuery(id+"F0.wireOp",EDGE,"E297"),sQuery(id+"F0.wireOp",EDGE,"E298"),sQuery(id+"F0.wireOp",EDGE,"E299"),sQuery(id+"F0.wireOp",EDGE,"E300"),sQuery(id+"F0.wireOp",EDGE,"E301"),sQuery(id+"F0.wireOp",EDGE,"E302"),sQuery(id+"F0.wireOp",EDGE,"E303"),sQuery(id+"F0.wireOp",EDGE,"E304"),sQuery(id+"F0.wireOp",EDGE,"E305"),sQuery(id+"F0.wireOp",EDGE,"E306"),sQuery(id+"F0.wireOp",EDGE,"E307"),sQuery(id+"F0.wireOp",EDGE,"E308"),sQuery(id+"F0.wireOp",EDGE,"E309"),sQuery(id+"F0.wireOp",EDGE,"E310"),sQuery(id+"F0.wireOp",EDGE,"E311"),sQuery(id+"F0.wireOp",EDGE,"E312"),sQuery(id+"F0.wireOp",EDGE,"E313"),sQuery(id+"F0.wireOp",EDGE,"E314"),sQuery(id+"F0.wireOp",EDGE,"E315"),sQuery(id+"F0.wireOp",EDGE,"E316"),sQuery(id+"F0.wireOp",EDGE,"E317"),sQuery(id+"F0.wireOp",EDGE,"E318"),sQuery(id+"F0.wireOp",EDGE,"E319"),sQuery(id+"F0.wireOp",EDGE,"E320"),sQuery(id+"F0.wireOp",EDGE,"E321"),sQuery(id+"F0.wireOp",EDGE,"E322"),sQuery(id+"F0.wireOp",EDGE,"E323"),sQuery(id+"F0.wireOp",EDGE,"E324"),sQuery(id+"F0.wireOp",EDGE,"E325"),sQuery(id+"F0.wireOp",EDGE,"E326"),sQuery(id+"F0.wireOp",EDGE,"E327"),sQuery(id+"F0.wireOp",EDGE,"E328"),sQuery(id+"F0.wireOp",EDGE,"E329"),sQuery(id+"F0.wireOp",EDGE,"E330"),sQuery(id+"F0.wireOp",EDGE,"E331"),sQuery(id+"F0.wireOp",EDGE,"E332"),sQuery(id+"F0.wireOp",EDGE,"E333"),sQuery(id+"F0.wireOp",EDGE,"E334"),sQuery(id+"F0.wireOp",EDGE,"E335"),sQuery(id+"F0.wireOp",EDGE,"E336"),sQuery(id+"F0.wireOp",EDGE,"E337"),sQuery(id+"F0.wireOp",EDGE,"E338"),sQuery(id+"F0.wireOp",EDGE,"E339"),sQuery(id+"F0.wireOp",EDGE,"E340"),sQuery(id+"F0.wireOp",EDGE,"E341"),sQuery(id+"F0.wireOp",EDGE,"E342")])]});
            transform(context, id + "F10", {"entities" : qUnion([Q0]), "transformType" : TransformType.TRANSLATION_3D, "dx" : -20 * mm, "dy" : 0 * mm, "dz" : 0 * mm, "makeCopy" : false});
        }
        {
            var Q0;
            Q0=makeQuery(id+"F1.opExtrude","SWEPT_BODY",BODY,{"disambiguationData":[OSD([sQuery(id+"F0.wireOp",EDGE,"E0"),sQuery(id+"F0.wireOp",EDGE,"E1"),sQuery(id+"F0.wireOp",EDGE,"E2"),sQuery(id+"F0.wireOp",EDGE,"E3"),sQuery(id+"F0.wireOp",EDGE,"E4"),sQuery(id+"F0.wireOp",EDGE,"E5"),sQuery(id+"F0.wireOp",EDGE,"E6"),sQuery(id+"F0.wireOp",EDGE,"E7"),sQuery(id+"F0.wireOp",EDGE,"E8"),sQuery(id+"F0.wireOp",EDGE,"E9"),sQuery(id+"F0.wireOp",EDGE,"d1f12e28-619d-48a0-af9d-363aaf069b2c"),sQuery(id+"F0.wireOp",EDGE,"8f1ad2f6-87f8-4d0a-9a6f-9509bc73a5d0"),sQuery(id+"F0.wireOp",EDGE,"b73132a2-273c-440c-8538-d33cb83e02cf"),sQuery(id+"F0.wireOp",EDGE,"5e68acf4-36c0-4116-82c0-8787465f5633"),sQuery(id+"F0.wireOp",EDGE,"0160ff8c-e588-4e40-a1a7-46cc7af3fc36"),sQuery(id+"F0.wireOp",EDGE,"75dd3127-571f-4835-931a-068837c7416e"),sQuery(id+"F0.wireOp",EDGE,"E10"),sQuery(id+"F0.wireOp",EDGE,"E11"),sQuery(id+"F0.wireOp",EDGE,"E12"),sQuery(id+"F0.wireOp",EDGE,"E13"),sQuery(id+"F0.wireOp",EDGE,"E14"),sQuery(id+"F0.wireOp",EDGE,"E15"),sQuery(id+"F0.wireOp",EDGE,"E16"),sQuery(id+"F0.wireOp",EDGE,"E17"),sQuery(id+"F0.wireOp",EDGE,"E18"),sQuery(id+"F0.wireOp",EDGE,"E19"),sQuery(id+"F0.wireOp",EDGE,"E20"),sQuery(id+"F0.wireOp",EDGE,"E21"),sQuery(id+"F0.wireOp",EDGE,"E22"),sQuery(id+"F0.wireOp",EDGE,"E23"),sQuery(id+"F0.wireOp",EDGE,"E24"),sQuery(id+"F0.wireOp",EDGE,"E25"),sQuery(id+"F0.wireOp",EDGE,"E26"),sQuery(id+"F0.wireOp",EDGE,"E27"),sQuery(id+"F0.wireOp",EDGE,"E28"),sQuery(id+"F0.wireOp",EDGE,"E29"),sQuery(id+"F0.wireOp",EDGE,"E30"),sQuery(id+"F0.wireOp",EDGE,"E31"),sQuery(id+"F0.wireOp",EDGE,"E32"),sQuery(id+"F0.wireOp",EDGE,"E33"),sQuery(id+"F0.wireOp",EDGE,"E34"),sQuery(id+"F0.wireOp",EDGE,"E35"),sQuery(id+"F0.wireOp",EDGE,"E36"),sQuery(id+"F0.wireOp",EDGE,"E37"),sQuery(id+"F0.wireOp",EDGE,"E38"),sQuery(id+"F0.wireOp",EDGE,"E39"),sQuery(id+"F0.wireOp",EDGE,"E40"),sQuery(id+"F0.wireOp",EDGE,"E41"),sQuery(id+"F0.wireOp",EDGE,"E42"),sQuery(id+"F0.wireOp",EDGE,"E43"),sQuery(id+"F0.wireOp",EDGE,"E44"),sQuery(id+"F0.wireOp",EDGE,"E45"),sQuery(id+"F0.wireOp",EDGE,"E46"),sQuery(id+"F0.wireOp",EDGE,"E47"),sQuery(id+"F0.wireOp",EDGE,"E48"),sQuery(id+"F0.wireOp",EDGE,"E49"),sQuery(id+"F0.wireOp",EDGE,"E50"),sQuery(id+"F0.wireOp",EDGE,"E51"),sQuery(id+"F0.wireOp",EDGE,"E52"),sQuery(id+"F0.wireOp",EDGE,"E53"),sQuery(id+"F0.wireOp",EDGE,"E54"),sQuery(id+"F0.wireOp",EDGE,"E55"),sQuery(id+"F0.wireOp",EDGE,"E56"),sQuery(id+"F0.wireOp",EDGE,"E57"),sQuery(id+"F0.wireOp",EDGE,"E58"),sQuery(id+"F0.wireOp",EDGE,"E59"),sQuery(id+"F0.wireOp",EDGE,"E60"),sQuery(id+"F0.wireOp",EDGE,"E61"),sQuery(id+"F0.wireOp",EDGE,"E62"),sQuery(id+"F0.wireOp",EDGE,"E63"),sQuery(id+"F0.wireOp",EDGE,"E64"),sQuery(id+"F0.wireOp",EDGE,"E65"),sQuery(id+"F0.wireOp",EDGE,"E66"),sQuery(id+"F0.wireOp",EDGE,"E67"),sQuery(id+"F0.wireOp",EDGE,"354140e0-899d-4b1a-bd6e-5b08e5c9ae55"),sQuery(id+"F0.wireOp",EDGE,"332aa9ae-4695-4afa-a665-cddeb38f0f21"),sQuery(id+"F0.wireOp",EDGE,"E68"),sQuery(id+"F0.wireOp",EDGE,"E69"),sQuery(id+"F0.wireOp",EDGE,"E70"),sQuery(id+"F0.wireOp",EDGE,"E71"),sQuery(id+"F0.wireOp",EDGE,"E72"),sQuery(id+"F0.wireOp",EDGE,"E73"),sQuery(id+"F0.wireOp",EDGE,"E74"),sQuery(id+"F0.wireOp",EDGE,"E75"),sQuery(id+"F0.wireOp",EDGE,"E76"),sQuery(id+"F0.wireOp",EDGE,"E77"),sQuery(id+"F0.wireOp",EDGE,"E78"),sQuery(id+"F0.wireOp",EDGE,"E79"),sQuery(id+"F0.wireOp",EDGE,"E80"),sQuery(id+"F0.wireOp",EDGE,"E81"),sQuery(id+"F0.wireOp",EDGE,"E82")])]});
            transform(context, id + "F11", {"entities" : qUnion([Q0]), "transformType" : TransformType.TRANSLATION_3D, "dx" : 10 * mm, "dy" : 0 * mm, "dz" : 0 * mm, "makeCopy" : false});
        }
        {
            var Q0;
            Q0=qCreatedBy(makeId("Top.planeOp"),FACE);
            var sketch = newSketch(context, id + "F12", { "sketchPlane" : qUnion([Q0])});
            skLineSegment(sketch, "E470", {"start": v(-85.56, 77.58) * mm, "end": v(-87.96, 77.58) * mm});
            skArc(sketch, "E471", {"start": v(-85.56, 77.58) * mm, "mid": v(-85.14, 77.75) * mm, "end": v(-84.96, 78.18) * mm});
            skLineSegment(sketch, "E472", {"start": v(-84.96, 79.58) * mm, "end": v(-84.96, 78.18) * mm});
            skLineSegment(sketch, "E473", {"start": v(-81.96, 79.58) * mm, "end": v(-84.96, 79.58) * mm});
            skLineSegment(sketch, "E474", {"start": v(-81.96, 78.18) * mm, "end": v(-81.96, 79.58) * mm});
            skArc(sketch, "E475", {"start": v(-81.96, 78.18) * mm, "mid": v(-81.78, 77.75) * mm, "end": v(-81.36, 77.58) * mm});
            skLineSegment(sketch, "E476", {"start": v(-79.56, 77.58) * mm, "end": v(-81.36, 77.58) * mm});
            skArc(sketch, "E477", {"start": v(-79.56, 77.58) * mm, "mid": v(-79.14, 77.75) * mm, "end": v(-78.96, 78.18) * mm});
            skLineSegment(sketch, "E478", {"start": v(-78.96, 79.58) * mm, "end": v(-78.96, 78.18) * mm});
            skLineSegment(sketch, "E479", {"start": v(-75.96, 79.58) * mm, "end": v(-78.96, 79.58) * mm});
            skLineSegment(sketch, "E480", {"start": v(-75.96, 78.18) * mm, "end": v(-75.96, 79.58) * mm});
            skArc(sketch, "E481", {"start": v(-75.96, 78.18) * mm, "mid": v(-75.78, 77.75) * mm, "end": v(-75.36, 77.58) * mm});
            skLineSegment(sketch, "E482", {"start": v(-71.56, 77.58) * mm, "end": v(-75.36, 77.58) * mm});
            skArc(sketch, "E483", {"start": v(-71.56, 77.58) * mm, "mid": v(-71.14, 77.75) * mm, "end": v(-70.96, 78.18) * mm});
            skLineSegment(sketch, "E484", {"start": v(-70.96, 81.98) * mm, "end": v(-70.96, 78.18) * mm});
            skArc(sketch, "E485", {"start": v(-70.96, 81.98) * mm, "mid": v(-71.14, 82.4) * mm, "end": v(-71.56, 82.58) * mm});
            skLineSegment(sketch, "E486", {"start": v(-72.96, 82.58) * mm, "end": v(-71.56, 82.58) * mm});
            skLineSegment(sketch, "E487", {"start": v(-72.96, 85.58) * mm, "end": v(-72.96, 82.58) * mm});
            skLineSegment(sketch, "E488", {"start": v(-71.56, 85.58) * mm, "end": v(-72.96, 85.58) * mm});
            skArc(sketch, "E489", {"start": v(-71.56, 85.58) * mm, "mid": v(-71.14, 85.75) * mm, "end": v(-70.96, 86.18) * mm});
            skLineSegment(sketch, "E490", {"start": v(-70.96, 87.98) * mm, "end": v(-70.96, 86.18) * mm});
            skArc(sketch, "E491", {"start": v(-70.96, 87.98) * mm, "mid": v(-71.14, 88.4) * mm, "end": v(-71.56, 88.58) * mm});
            skLineSegment(sketch, "E492", {"start": v(-72.96, 88.58) * mm, "end": v(-71.56, 88.58) * mm});
            skLineSegment(sketch, "E493", {"start": v(-72.96, 91.58) * mm, "end": v(-72.96, 88.58) * mm});
            skLineSegment(sketch, "E494", {"start": v(-71.56, 91.58) * mm, "end": v(-72.96, 91.58) * mm});
            skArc(sketch, "E495", {"start": v(-71.56, 91.58) * mm, "mid": v(-71.14, 91.75) * mm, "end": v(-70.96, 92.18) * mm});
            skLineSegment(sketch, "E496", {"start": v(-70.96, 93.98) * mm, "end": v(-70.96, 92.18) * mm});
            skArc(sketch, "E497", {"start": v(-70.96, 93.98) * mm, "mid": v(-71.14, 94.4) * mm, "end": v(-71.56, 94.58) * mm});
            skLineSegment(sketch, "E498", {"start": v(-72.96, 94.58) * mm, "end": v(-71.56, 94.58) * mm});
            skLineSegment(sketch, "E499", {"start": v(-72.96, 97.58) * mm, "end": v(-72.96, 94.58) * mm});
            skLineSegment(sketch, "E500", {"start": v(-71.56, 97.58) * mm, "end": v(-72.96, 97.58) * mm});
            skArc(sketch, "E501", {"start": v(-71.56, 97.58) * mm, "mid": v(-71.14, 97.75) * mm, "end": v(-70.96, 98.18) * mm});
            skLineSegment(sketch, "E502", {"start": v(-70.96, 99.58) * mm, "end": v(-70.96, 98.18) * mm});
            skLineSegment(sketch, "E503", {"start": v(-6.3, -12.42) * mm, "end": v(-70.96, 99.58) * mm});
            skArc(sketch, "E504", {"start": v(-11.35, -23.42) * mm, "mid": v(-5.98, -19.23) * mm, "end": v(-6.3, -12.42) * mm});
            skArc(sketch, "E505", {"start": v(-12.38, -21.7) * mm, "mid": v(-12.72, -23.08) * mm, "end": v(-11.35, -23.42) * mm});
            skArc(sketch, "E506", {"start": v(-12.38, -21.7) * mm, "mid": v(-14.96, -12.42) * mm, "end": v(-17.53, -21.7) * mm});
            skArc(sketch, "E507", {"start": v(-18.56, -23.42) * mm, "mid": v(-17.2, -23.08) * mm, "end": v(-17.53, -21.7) * mm});
            skArc(sketch, "E508", {"start": v(-23.03, -11.73) * mm, "mid": v(-23.62, -18.65) * mm, "end": v(-18.56, -23.42) * mm});
            skArc(sketch, "E509", {"start": v(-23.03, -11.73) * mm, "mid": v(-21.66, -7.29) * mm, "end": v(-22.44, -2.71) * mm});
            skArc(sketch, "E510", {"start": v(-22.44, -2.71) * mm, "mid": v(-40.14, 31.05) * mm, "end": v(-62.96, 61.58) * mm});
            skArc(sketch, "E511", {"start": v(-62.96, 61.58) * mm, "mid": v(-73.6, 69.43) * mm, "end": v(-86.23, 73.38) * mm});
            skArc(sketch, "E512", {"start": v(-87.96, 75.36) * mm, "mid": v(-87.47, 74.04) * mm, "end": v(-86.23, 73.38) * mm});
            skLineSegment(sketch, "E513", {"start": v(-87.96, 77.58) * mm, "end": v(-87.96, 75.36) * mm});
            skLineSegment(sketch, "E514", {"start": v(-5.34, 45.8) * mm, "end": v(-5.34, 49.8) * mm});
            skLineSegment(sketch, "E515", {"start": v(-5.34, 49.8) * mm, "end": v(-7.59, 49.8) * mm});
            skLineSegment(sketch, "E516", {"start": v(-7.59, 49.8) * mm, "end": v(-7.59, 45.8) * mm});
            skLineSegment(sketch, "E517", {"start": v(-7.59, 45.8) * mm, "end": v(-5.34, 45.8) * mm});
            skLineSegment(sketch, "E518", {"start": v(83.41, 39.8) * mm, "end": v(83.41, 43.8) * mm});
            skLineSegment(sketch, "E519", {"start": v(83.41, 43.8) * mm, "end": v(81.16, 43.8) * mm});
            skLineSegment(sketch, "E520", {"start": v(81.16, 43.8) * mm, "end": v(81.16, 39.8) * mm});
            skLineSegment(sketch, "E521", {"start": v(81.16, 39.8) * mm, "end": v(83.41, 39.8) * mm});
            skLineSegment(sketch, "E522", {"start": v(85.91, 37.3) * mm, "end": v(85.91, 52.3) * mm});
            skLineSegment(sketch, "E523", {"start": v(-10.09, 37.3) * mm, "end": v(85.91, 37.3) * mm});
            skLineSegment(sketch, "E524", {"start": v(-10.09, 52.3) * mm, "end": v(-10.09, 37.3) * mm});
            skLineSegment(sketch, "E525", {"start": v(85.91, 52.3) * mm, "end": v(-10.09, 52.3) * mm});
            skLineSegment(sketch, "E526", {"start": v(83.41, 49.8) * mm, "end": v(81.16, 49.8) * mm});
            skLineSegment(sketch, "E527", {"start": v(81.16, 49.8) * mm, "end": v(81.16, 45.8) * mm});
            skLineSegment(sketch, "E528", {"start": v(81.16, 45.8) * mm, "end": v(83.41, 45.8) * mm});
            skLineSegment(sketch, "E529", {"start": v(83.41, 45.8) * mm, "end": v(83.41, 49.8) * mm});
            skLineSegment(sketch, "E530", {"start": v(-5.34, 39.8) * mm, "end": v(-5.34, 43.8) * mm});
            skLineSegment(sketch, "E531", {"start": v(-5.34, 43.8) * mm, "end": v(-7.59, 43.8) * mm});
            skLineSegment(sketch, "E532", {"start": v(-7.59, 43.8) * mm, "end": v(-7.59, 39.8) * mm});
            skLineSegment(sketch, "E533", {"start": v(-7.59, 39.8) * mm, "end": v(-5.34, 39.8) * mm});
            skArc(sketch, "E534", {"start": v(15.38, -4.78) * mm, "mid": v(15.84, -4.82) * mm, "end": v(16.19, -4.53) * mm});
            skLineSegment(sketch, "E535", {"start": v(16.19, -4.53) * mm, "end": v(17.5, -2.06) * mm});
            skArc(sketch, "E536", {"start": v(17.5, -2.06) * mm, "mid": v(17.55, -1.6) * mm, "end": v(17.26, -1.25) * mm});
            skLineSegment(sketch, "E537", {"start": v(17.26, -1.25) * mm, "end": v(16.55, -0.87) * mm});
            skArc(sketch, "E538", {"start": v(16.55, -0.87) * mm, "mid": v(16.1, -0.83) * mm, "end": v(15.74, -1.12) * mm});
            skLineSegment(sketch, "E539", {"start": v(15.74, -1.12) * mm, "end": v(14.42, -3.6) * mm});
            skArc(sketch, "E540", {"start": v(14.42, -3.6) * mm, "mid": v(14.38, -4.05) * mm, "end": v(14.67, -4.4) * mm});
            skLineSegment(sketch, "E541", {"start": v(14.67, -4.4) * mm, "end": v(15.38, -4.78) * mm});
            skLineSegment(sketch, "E542", {"start": v(10.56, -15.13) * mm, "end": v(11.87, -12.65) * mm});
            skArc(sketch, "E543", {"start": v(11.87, -12.65) * mm, "mid": v(11.91, -12.2) * mm, "end": v(11.62, -11.84) * mm});
            skLineSegment(sketch, "E544", {"start": v(11.62, -11.84) * mm, "end": v(10.92, -11.47) * mm});
            skArc(sketch, "E545", {"start": v(10.92, -11.47) * mm, "mid": v(10.46, -11.42) * mm, "end": v(10.1, -11.71) * mm});
            skLineSegment(sketch, "E546", {"start": v(10.1, -11.71) * mm, "end": v(8.79, -14.19) * mm});
            skArc(sketch, "E547", {"start": v(8.79, -14.19) * mm, "mid": v(8.75, -14.64) * mm, "end": v(9.04, -15) * mm});
            skLineSegment(sketch, "E548", {"start": v(9.04, -15) * mm, "end": v(9.74, -15.37) * mm});
            skArc(sketch, "E549", {"start": v(9.74, -15.37) * mm, "mid": v(10.2, -15.42) * mm, "end": v(10.56, -15.13) * mm});
            skArc(sketch, "E550", {"start": v(92.35, -9.7) * mm, "mid": v(92.64, -9.35) * mm, "end": v(92.6, -8.89) * mm});
            skLineSegment(sketch, "E551", {"start": v(92.6, -8.89) * mm, "end": v(91.28, -6.42) * mm});
            skArc(sketch, "E552", {"start": v(91.28, -6.42) * mm, "mid": v(90.93, -6.12) * mm, "end": v(90.47, -6.17) * mm});
            skLineSegment(sketch, "E553", {"start": v(90.47, -6.17) * mm, "end": v(89.76, -6.54) * mm});
            skArc(sketch, "E554", {"start": v(89.76, -6.54) * mm, "mid": v(89.47, -6.9) * mm, "end": v(89.51, -7.36) * mm});
            skLineSegment(sketch, "E555", {"start": v(89.51, -7.36) * mm, "end": v(90.83, -9.83) * mm});
            skArc(sketch, "E556", {"start": v(90.83, -9.83) * mm, "mid": v(91.18, -10.12) * mm, "end": v(91.64, -10.08) * mm});
            skLineSegment(sketch, "E557", {"start": v(91.64, -10.08) * mm, "end": v(92.35, -9.7) * mm});
            skLineSegment(sketch, "E558", {"start": v(89.77, 0.68) * mm, "end": v(14.43, 0.68) * mm});
            skLineSegment(sketch, "E559", {"start": v(100.1, -18.75) * mm, "end": v(89.77, 0.68) * mm});
            skLineSegment(sketch, "E560", {"start": v(4.1, -18.75) * mm, "end": v(100.1, -18.75) * mm});
            skLineSegment(sketch, "E561", {"start": v(14.43, 0.68) * mm, "end": v(4.1, -18.75) * mm});
            skLineSegment(sketch, "E562", {"start": v(95.41, -14.19) * mm, "end": v(94.1, -11.71) * mm});
            skArc(sketch, "E563", {"start": v(94.1, -11.71) * mm, "mid": v(93.74, -11.42) * mm, "end": v(93.29, -11.47) * mm});
            skLineSegment(sketch, "E564", {"start": v(93.29, -11.47) * mm, "end": v(92.58, -11.84) * mm});
            skArc(sketch, "E565", {"start": v(92.58, -11.84) * mm, "mid": v(92.29, -12.2) * mm, "end": v(92.33, -12.65) * mm});
            skLineSegment(sketch, "E566", {"start": v(92.33, -12.65) * mm, "end": v(93.65, -15.13) * mm});
            skArc(sketch, "E567", {"start": v(93.65, -15.13) * mm, "mid": v(94, -15.42) * mm, "end": v(94.46, -15.37) * mm});
            skLineSegment(sketch, "E568", {"start": v(94.46, -15.37) * mm, "end": v(95.16, -15) * mm});
            skArc(sketch, "E569", {"start": v(95.16, -15) * mm, "mid": v(95.46, -14.64) * mm, "end": v(95.41, -14.19) * mm});
            skLineSegment(sketch, "E570", {"start": v(87.65, -0.87) * mm, "end": v(86.95, -1.25) * mm});
            skArc(sketch, "E571", {"start": v(86.95, -1.25) * mm, "mid": v(86.65, -1.6) * mm, "end": v(86.7, -2.06) * mm});
            skLineSegment(sketch, "E572", {"start": v(86.7, -2.06) * mm, "end": v(88.01, -4.53) * mm});
            skArc(sketch, "E573", {"start": v(88.01, -4.53) * mm, "mid": v(88.37, -4.82) * mm, "end": v(88.82, -4.78) * mm});
            skLineSegment(sketch, "E574", {"start": v(88.82, -4.78) * mm, "end": v(89.53, -4.4) * mm});
            skArc(sketch, "E575", {"start": v(89.53, -4.4) * mm, "mid": v(89.82, -4.05) * mm, "end": v(89.78, -3.6) * mm});
            skLineSegment(sketch, "E576", {"start": v(89.78, -3.6) * mm, "end": v(88.46, -1.12) * mm});
            skArc(sketch, "E577", {"start": v(88.46, -1.12) * mm, "mid": v(88.1, -0.83) * mm, "end": v(87.65, -0.87) * mm});
            skLineSegment(sketch, "E578", {"start": v(13.37, -9.83) * mm, "end": v(14.69, -7.36) * mm});
            skArc(sketch, "E579", {"start": v(14.69, -7.36) * mm, "mid": v(14.73, -6.9) * mm, "end": v(14.44, -6.54) * mm});
            skLineSegment(sketch, "E580", {"start": v(14.44, -6.54) * mm, "end": v(13.73, -6.17) * mm});
            skArc(sketch, "E581", {"start": v(13.73, -6.17) * mm, "mid": v(13.28, -6.12) * mm, "end": v(12.92, -6.42) * mm});
            skLineSegment(sketch, "E582", {"start": v(12.92, -6.42) * mm, "end": v(11.6, -8.89) * mm});
            skArc(sketch, "E583", {"start": v(11.6, -8.89) * mm, "mid": v(11.56, -9.35) * mm, "end": v(11.85, -9.7) * mm});
            skLineSegment(sketch, "E584", {"start": v(11.85, -9.7) * mm, "end": v(12.56, -10.08) * mm});
            skArc(sketch, "E585", {"start": v(12.56, -10.08) * mm, "mid": v(13.02, -10.12) * mm, "end": v(13.37, -9.83) * mm});
            skArc(sketch, "E586", {"start": v(-87.87, -97.72) * mm, "mid": v(-88.21, -99.1) * mm, "end": v(-86.84, -99.43) * mm});
            skArc(sketch, "E587", {"start": v(-87.87, -97.72) * mm, "mid": v(-90.45, -88.43) * mm, "end": v(-93.02, -97.72) * mm});
            skArc(sketch, "E588", {"start": v(-94.05, -99.43) * mm, "mid": v(-92.68, -99.1) * mm, "end": v(-93.02, -97.72) * mm});
            skArc(sketch, "E589", {"start": v(-99.1, -88.43) * mm, "mid": v(-99.42, -95.24) * mm, "end": v(-94.05, -99.43) * mm});
            skLineSegment(sketch, "E590", {"start": v(-95.87, -82.82) * mm, "end": v(-99.1, -88.43) * mm});
            skArc(sketch, "E591", {"start": v(-81.16, -65.79) * mm, "mid": v(-89.32, -73.61) * mm, "end": v(-95.87, -82.82) * mm});
            skArc(sketch, "E592", {"start": v(80.26, -65.79) * mm, "mid": v(-0.45, -37.7) * mm, "end": v(-81.16, -65.79) * mm});
            skArc(sketch, "E593", {"start": v(94.97, -82.82) * mm, "mid": v(88.43, -73.61) * mm, "end": v(80.26, -65.79) * mm});
            skLineSegment(sketch, "E594", {"start": v(98.21, -88.43) * mm, "end": v(94.97, -82.82) * mm});
            skArc(sketch, "E595", {"start": v(93.16, -99.43) * mm, "mid": v(98.53, -95.24) * mm, "end": v(98.21, -88.43) * mm});
            skArc(sketch, "E596", {"start": v(92.13, -97.72) * mm, "mid": v(91.79, -99.1) * mm, "end": v(93.16, -99.43) * mm});
            skArc(sketch, "E597", {"start": v(92.13, -97.72) * mm, "mid": v(89.55, -88.43) * mm, "end": v(86.98, -97.72) * mm});
            skArc(sketch, "E598", {"start": v(85.95, -99.43) * mm, "mid": v(87.32, -99.1) * mm, "end": v(86.98, -97.72) * mm});
            skArc(sketch, "E599", {"start": v(81.48, -87.74) * mm, "mid": v(80.9, -94.66) * mm, "end": v(85.95, -99.43) * mm});
            skArc(sketch, "E600", {"start": v(81.48, -87.74) * mm, "mid": v(82.55, -85.14) * mm, "end": v(82.87, -82.34) * mm});
            skArc(sketch, "E601", {"start": v(82.87, -82.34) * mm, "mid": v(82.2, -79.59) * mm, "end": v(80.51, -77.32) * mm});
            skArc(sketch, "E602", {"start": v(80.51, -77.32) * mm, "mid": v(-0.45, -46.58) * mm, "end": v(-81.4, -77.32) * mm});
            skArc(sketch, "E603", {"start": v(-81.4, -77.32) * mm, "mid": v(-83.1, -79.59) * mm, "end": v(-83.76, -82.34) * mm});
            skArc(sketch, "E604", {"start": v(-83.76, -82.34) * mm, "mid": v(-83.45, -85.14) * mm, "end": v(-82.37, -87.74) * mm});
            skArc(sketch, "E605", {"start": v(-86.84, -99.43) * mm, "mid": v(-81.78, -94.66) * mm, "end": v(-82.37, -87.74) * mm});
            skSolve(sketch);
        }
        {
            var Q0;
            Q0 = qSketchRegion(id + "F12", true);
            extrude(context, id + "F13", {"entities" : qUnion([Q0]), "depth" : 1.5 * mm});
        }
        {
            var Q0;
            Q0=qCreatedBy(makeId("Top.planeOp"),FACE);
            var sketch = newSketch(context, id + "F14", { "sketchPlane" : qUnion([Q0])});
            skLineSegment(sketch, "E606.bottom", {"start": v(-128.22, 241.55) * mm, "end": v(-88.62, 241.55) * mm});
            skLineSegment(sketch, "E606.top", {"start": v(-128.22, 199.55) * mm, "end": v(-88.62, 199.55) * mm});
            skLineSegment(sketch, "E606.left", {"start": v(-129.42, 240.35) * mm, "end": v(-129.42, 200.75) * mm});
            skLineSegment(sketch, "E606.right", {"start": v(-87.42, 240.35) * mm, "end": v(-87.42, 200.75) * mm});
            skPoint(sketch, "E607.visualSharp", {"position": v(-129.42, 241.55) * mm});
            skArc(sketch, "E607.filletArc", {"start": v(-128.22, 241.55) * mm, "mid": v(-129.07, 241.2) * mm, "end": v(-129.42, 240.35) * mm});
            skPoint(sketch, "E608.visualSharp", {"position": v(-87.42, 241.55) * mm});
            skArc(sketch, "E608.filletArc", {"start": v(-87.42, 240.35) * mm, "mid": v(-87.77, 241.2) * mm, "end": v(-88.62, 241.55) * mm});
            skPoint(sketch, "E609.visualSharp", {"position": v(-87.42, 199.55) * mm});
            skArc(sketch, "E609.filletArc", {"start": v(-88.62, 199.55) * mm, "mid": v(-87.77, 199.9) * mm, "end": v(-87.42, 200.75) * mm});
            skPoint(sketch, "E610.visualSharp", {"position": v(-129.42, 199.55) * mm});
            skArc(sketch, "E610.filletArc", {"start": v(-129.42, 200.75) * mm, "mid": v(-129.07, 199.9) * mm, "end": v(-128.22, 199.55) * mm});
            skSolve(sketch);
        }
        {
            var Q0;
            Q0 = qSketchRegion(id + "F14", true);
            extrude(context, id + "F15", {"entities" : qUnion([Q0]), "depth" : 1 * mm});
        }
        {
            var Q0;
            Q0=qCreatedBy(makeId("Top.planeOp"),FACE);
            var sketch = newSketch(context, id + "F16", { "sketchPlane" : qUnion([Q0])});
            skLineSegment(sketch, "E611.bottom", {"start": v(-21.69, 237.17) * mm, "end": v(17.91, 237.17) * mm});
            skLineSegment(sketch, "E611.top", {"start": v(-21.69, 134.17) * mm, "end": v(17.91, 134.17) * mm});
            skLineSegment(sketch, "E611.left", {"start": v(-22.89, 235.97) * mm, "end": v(-22.89, 135.37) * mm});
            skLineSegment(sketch, "E611.right", {"start": v(19.11, 235.97) * mm, "end": v(19.11, 135.37) * mm});
            skLineSegment(sketch, "E612.bottom", {"start": v(57.54, 214.74) * mm, "end": v(85.14, 214.74) * mm});
            skLineSegment(sketch, "E612.top", {"start": v(57.54, 170.74) * mm, "end": v(85.14, 170.74) * mm});
            skLineSegment(sketch, "E612.left", {"start": v(56.34, 213.54) * mm, "end": v(56.34, 171.94) * mm});
            skLineSegment(sketch, "E612.right", {"start": v(86.34, 213.54) * mm, "end": v(86.34, 171.94) * mm});
            skPoint(sketch, "E613.visualSharp", {"position": v(-22.89, 237.17) * mm});
            skArc(sketch, "E613.filletArc", {"start": v(-21.69, 237.17) * mm, "mid": v(-22.54, 236.82) * mm, "end": v(-22.89, 235.97) * mm});
            skPoint(sketch, "E614.visualSharp", {"position": v(19.11, 237.17) * mm});
            skArc(sketch, "E614.filletArc", {"start": v(19.11, 235.97) * mm, "mid": v(18.76, 236.82) * mm, "end": v(17.91, 237.17) * mm});
            skPoint(sketch, "E615.visualSharp", {"position": v(19.11, 134.17) * mm});
            skArc(sketch, "E615.filletArc", {"start": v(17.91, 134.17) * mm, "mid": v(18.76, 134.52) * mm, "end": v(19.11, 135.37) * mm});
            skPoint(sketch, "E616.visualSharp", {"position": v(-22.89, 134.17) * mm});
            skArc(sketch, "E616.filletArc", {"start": v(-22.89, 135.37) * mm, "mid": v(-22.54, 134.52) * mm, "end": v(-21.69, 134.17) * mm});
            skPoint(sketch, "E617.visualSharp", {"position": v(56.34, 214.74) * mm});
            skArc(sketch, "E617.filletArc", {"start": v(57.54, 214.74) * mm, "mid": v(56.7, 214.39) * mm, "end": v(56.34, 213.54) * mm});
            skPoint(sketch, "E618.visualSharp", {"position": v(86.34, 214.74) * mm});
            skArc(sketch, "E618.filletArc", {"start": v(86.34, 213.54) * mm, "mid": v(86, 214.39) * mm, "end": v(85.14, 214.74) * mm});
            skPoint(sketch, "E619.visualSharp", {"position": v(86.34, 170.74) * mm});
            skArc(sketch, "E619.filletArc", {"start": v(85.14, 170.74) * mm, "mid": v(86, 171.09) * mm, "end": v(86.34, 171.94) * mm});
            skPoint(sketch, "E620.visualSharp", {"position": v(56.34, 170.74) * mm});
            skArc(sketch, "E620.filletArc", {"start": v(56.34, 171.94) * mm, "mid": v(56.7, 171.09) * mm, "end": v(57.54, 170.74) * mm});
            skSolve(sketch);
        }
        {
            var Q0;
            Q0 = qSketchRegion(id + "F16", true);
            extrude(context, id + "F17", {"entities" : qUnion([Q0]), "depth" : 1 * mm});
        }
    });
